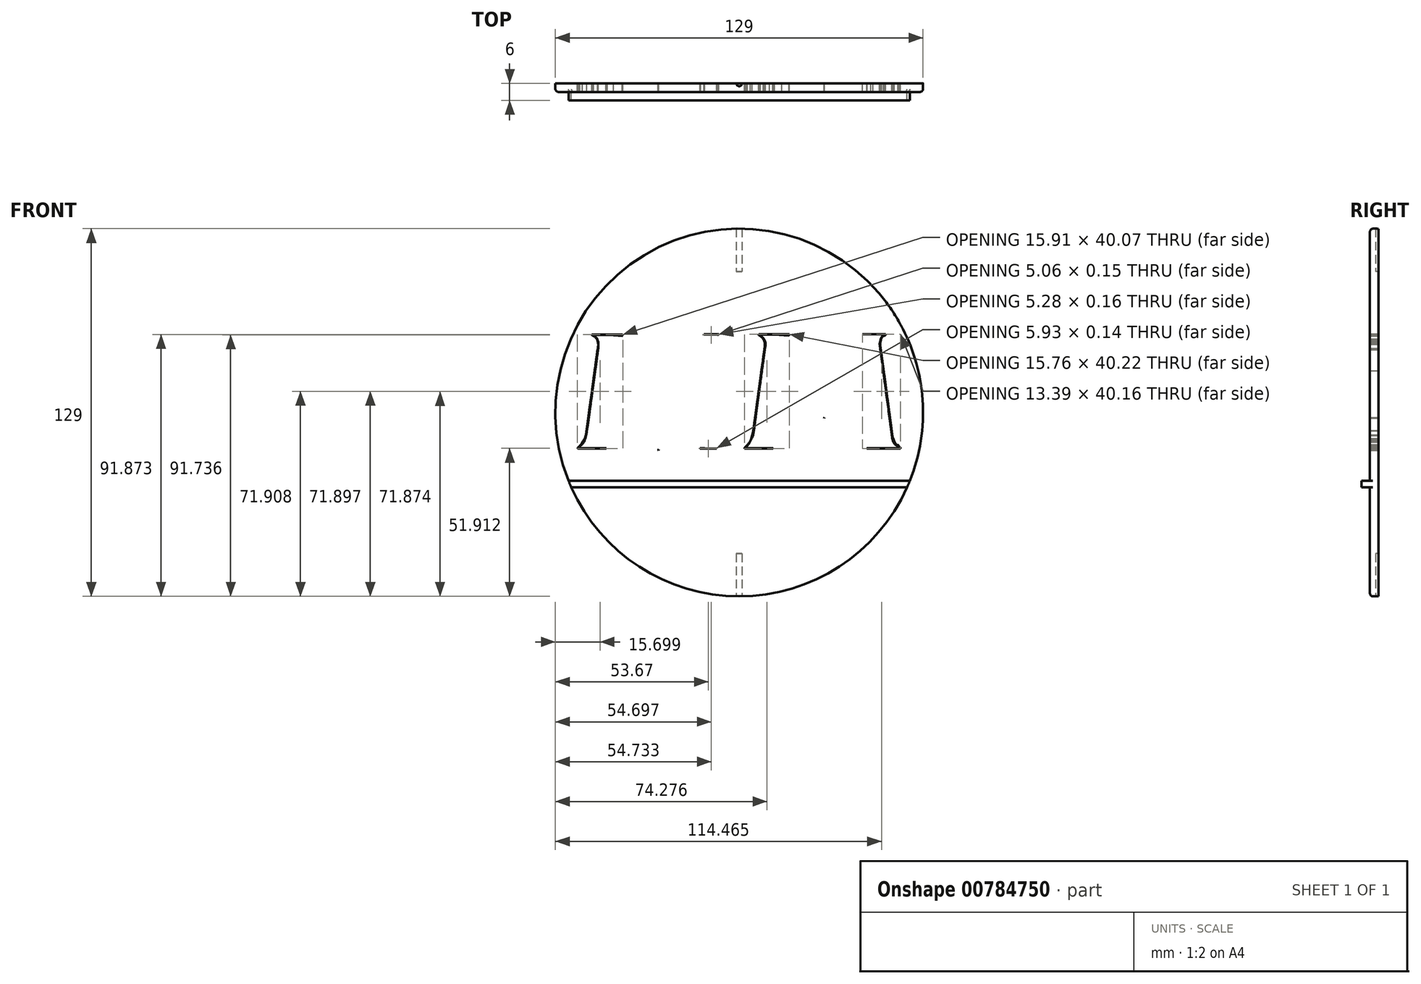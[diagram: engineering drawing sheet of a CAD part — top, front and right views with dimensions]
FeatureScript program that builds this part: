
annotation { "Feature Type Name" : "Feature", "Feature Type Description" : "" }
export const myFeature = defineFeature(function(context is Context, id is Id, definition is map)
    precondition{}
    {
        {
            var Q0;
            Q0=qCreatedBy(makeId("Front.planeOp"),FACE);
            var sketch = newSketch(context, id + "F0", { "sketchPlane" : qUnion([Q0])});
            skLineSegment(sketch, "E0", {"start": v(-46.61, -12.5) * mm, "end": v(-46.61, -12.63) * mm});
            skLineSegment(sketch, "E1", {"start": v(-46.61, -12.63) * mm, "end": v(-51.61, -12.65) * mm});
            skLineSegment(sketch, "E2", {"start": v(-51.61, -12.65) * mm, "end": v(-56.61, -12.66) * mm});
            skLineSegment(sketch, "E3", {"start": v(-56.61, -12.66) * mm, "end": v(-56.7, -12.53) * mm});
            skLineSegment(sketch, "E4", {"start": v(-56.7, -12.53) * mm, "end": v(-46.61, -12.5) * mm});
            skLineSegment(sketch, "E5", {"start": v(-51.66, 27.28) * mm, "end": v(-51.64, 27.4) * mm});
            skLineSegment(sketch, "E6", {"start": v(-51.64, 27.4) * mm, "end": v(-46.26, 27.4) * mm});
            skLineSegment(sketch, "E7", {"start": v(-46.26, 27.4) * mm, "end": v(-40.89, 27.4) * mm});
            skLineSegment(sketch, "E8", {"start": v(-40.89, 27.4) * mm, "end": v(-40.85, 27.03) * mm});
            skLineSegment(sketch, "E9", {"start": v(-40.85, 27.03) * mm, "end": v(-51.66, 27.28) * mm});
            skLineSegment(sketch, "E10", {"start": v(-12.4, 27.45) * mm, "end": v(-7.13, 27.44) * mm});
            skLineSegment(sketch, "E11", {"start": v(-7.13, 27.44) * mm, "end": v(-7.13, 27.3) * mm});
            skLineSegment(sketch, "E12", {"start": v(-7.13, 27.3) * mm, "end": v(-12.4, 27.45) * mm});
            skLineSegment(sketch, "E13", {"start": v(-7.87, -12.66) * mm, "end": v(-13.8, -12.66) * mm});
            skLineSegment(sketch, "E14", {"start": v(-13.8, -12.66) * mm, "end": v(-13.8, -12.52) * mm});
            skLineSegment(sketch, "E15", {"start": v(-13.8, -12.52) * mm, "end": v(-7.87, -12.66) * mm});
            skLineSegment(sketch, "E16", {"start": v(-28.9, -13) * mm, "end": v(-28.9, -13) * mm});
            skLineSegment(sketch, "E17", {"start": v(-7.56, 27.16) * mm, "end": v(-7.28, 27.3) * mm});
            skLineSegment(sketch, "E18", {"start": v(-7.28, 27.3) * mm, "end": v(-12.33, 27.3) * mm});
            skLineSegment(sketch, "E19", {"start": v(-12.33, 27.3) * mm, "end": v(-7.56, 27.16) * mm});
            skLineSegment(sketch, "E20", {"start": v(-41, 26.8) * mm, "end": v(-41.07, 27.3) * mm});
            skLineSegment(sketch, "E21", {"start": v(-41.07, 27.3) * mm, "end": v(-46.25, 27.3) * mm});
            skLineSegment(sketch, "E22", {"start": v(-46.25, 27.3) * mm, "end": v(-41, 26.8) * mm});
            skLineSegment(sketch, "E23", {"start": v(-28.47, -13.11) * mm, "end": v(-28.32, -13.24) * mm});
            skLineSegment(sketch, "E24", {"start": v(-28.32, -13.24) * mm, "end": v(-28.19, -12.9) * mm});
            skLineSegment(sketch, "E25", {"start": v(-28.19, -12.9) * mm, "end": v(-28.47, -13.11) * mm});
            skLineSegment(sketch, "E26", {"start": v(-27.92, -12.22) * mm, "end": v(-27.92, -12.22) * mm});
            skLineSegment(sketch, "E27", {"start": v(11.92, -12.5) * mm, "end": v(11.93, -12.66) * mm});
            skLineSegment(sketch, "E28", {"start": v(11.93, -12.66) * mm, "end": v(6.92, -12.65) * mm});
            skLineSegment(sketch, "E29", {"start": v(6.92, -12.65) * mm, "end": v(1.9, -12.63) * mm});
            skLineSegment(sketch, "E30", {"start": v(1.9, -12.63) * mm, "end": v(1.9, -12.5) * mm});
            skLineSegment(sketch, "E31", {"start": v(1.9, -12.5) * mm, "end": v(11.92, -12.5) * mm});
            skLineSegment(sketch, "E32", {"start": v(12.43, 27.44) * mm, "end": v(17.65, 27.44) * mm});
            skLineSegment(sketch, "E33", {"start": v(17.65, 27.44) * mm, "end": v(17.66, 27.2) * mm});
            skLineSegment(sketch, "E34", {"start": v(17.66, 27.2) * mm, "end": v(12.43, 27.44) * mm});
            skLineSegment(sketch, "E35", {"start": v(29.76, -1.83) * mm, "end": v(29.82, -2) * mm});
            skLineSegment(sketch, "E36", {"start": v(29.82, -2) * mm, "end": v(29.9, -1.79) * mm});
            skLineSegment(sketch, "E37", {"start": v(29.9, -1.79) * mm, "end": v(29.76, -1.83) * mm});
            skLineSegment(sketch, "E38", {"start": v(46.15, 27.45) * mm, "end": v(51.38, 27.44) * mm});
            skLineSegment(sketch, "E39", {"start": v(51.38, 27.44) * mm, "end": v(51.38, 27.3) * mm});
            skLineSegment(sketch, "E40", {"start": v(51.38, 27.3) * mm, "end": v(46.15, 27.45) * mm});
            skLineSegment(sketch, "E41", {"start": v(50.66, -12.65) * mm, "end": v(44.75, -12.63) * mm});
            skLineSegment(sketch, "E42", {"start": v(44.75, -12.63) * mm, "end": v(44.75, -12.5) * mm});
            skLineSegment(sketch, "E43", {"start": v(44.75, -12.5) * mm, "end": v(50.66, -12.65) * mm});
            skLineSegment(sketch, "E44", {"start": v(29.52, -12.91) * mm, "end": v(29.52, -12.91) * mm});
            skLineSegment(sketch, "E45", {"start": v(17.5, 26.99) * mm, "end": v(17.46, 27.32) * mm});
            skLineSegment(sketch, "E46", {"start": v(17.46, 27.32) * mm, "end": v(12.27, 27.32) * mm});
            skLineSegment(sketch, "E47", {"start": v(12.27, 27.32) * mm, "end": v(17.5, 26.99) * mm});
            skLineSegment(sketch, "E48", {"start": v(31.19, -10.73) * mm, "end": v(31.19, -10.73) * mm});
            skLineSegment(sketch, "E49", {"start": v(55.74, -11.44) * mm, "end": v(55.74, -11.44) * mm});
            skLineSegment(sketch, "E50", {"start": v(51.1, -23.94) * mm, "end": v(-0.4, -23.94) * mm});
            skLineSegment(sketch, "E51", {"start": v(-0.4, -23.94) * mm, "end": v(-51.9, -23.94) * mm});
            skFitSpline(sketch, "E52", {"points": [v(48.84, 42.11) * mm, v(51.52, 39.05) * mm, v(54.57, 34.66) * mm, v(56.48, 31.12) * mm]});
            skFitSpline(sketch, "E53", {"points": [v(57.39, 29.43) * mm, v(61.46, 21.5) * mm, v(63.83, 12.79) * mm, v(64.36, 3.78) * mm]});
            skFitSpline(sketch, "E54", {"points": [v(-28.9, -13) * mm, v(-29.65, -12.4) * mm, v(-31.06, -10.96) * mm, v(-31.47, -10.38) * mm]});
            skFitSpline(sketch, "E55", {"points": [v(-31.47, -10.38) * mm, v(-32.14, -9.4) * mm, v(-32.78, -8.19) * mm, v(-33.58, -6.32) * mm]});
            skFitSpline(sketch, "E56", {"points": [v(-33.58, -6.32) * mm, v(-33.81, -5.77) * mm, v(-34.06, -5.2) * mm, v(-34.12, -5.06) * mm]});
            skFitSpline(sketch, "E57", {"points": [v(-34.12, -5.06) * mm, v(-34.24, -4.8) * mm, v(-35.12, -2.7) * mm, v(-35.43, -1.93) * mm]});
            skFitSpline(sketch, "E58", {"points": [v(-35.43, -1.93) * mm, v(-35.52, -1.7) * mm, v(-35.64, -1.45) * mm, v(-35.68, -1.35) * mm]});
            skFitSpline(sketch, "E59", {"points": [v(-35.68, -1.35) * mm, v(-35.73, -1.25) * mm, v(-35.85, -0.95) * mm, v(-35.97, -0.68) * mm]});
            skFitSpline(sketch, "E60", {"points": [v(-35.97, -0.68) * mm, v(-36.36, 0.28) * mm, v(-37.63, 3.3) * mm, v(-37.86, 3.82) * mm]});
            skFitSpline(sketch, "E61", {"points": [v(-37.86, 3.82) * mm, v(-37.93, 3.97) * mm, v(-38.03, 4.22) * mm, v(-38.1, 4.38) * mm]});
            skFitSpline(sketch, "E62", {"points": [v(-38.1, 4.38) * mm, v(-38.16, 4.54) * mm, v(-38.42, 5.17) * mm, v(-38.68, 5.78) * mm]});
            skFitSpline(sketch, "E63", {"points": [v(-38.68, 5.78) * mm, v(-39.72, 8.24) * mm, v(-40.1, 9.15) * mm, v(-40.39, 9.84) * mm]});
            skFitSpline(sketch, "E64", {"points": [v(-40.39, 9.84) * mm, v(-41.15, 11.67) * mm, v(-41.63, 12.8) * mm, v(-41.68, 12.85) * mm]});
            skFitSpline(sketch, "E65", {"points": [v(-41.68, 12.85) * mm, v(-41.7, 12.88) * mm, v(-41.73, 12.95) * mm, v(-41.74, 13) * mm]});
            skFitSpline(sketch, "E66", {"points": [v(-41.74, 13) * mm, v(-41.74, 13.05) * mm, v(-41.79, 13.2) * mm, v(-41.85, 13.32) * mm]});
            skFitSpline(sketch, "E67", {"points": [v(-41.85, 13.32) * mm, v(-41.91, 13.45) * mm, v(-41.96, 13.58) * mm, v(-41.97, 13.6) * mm]});
            skFitSpline(sketch, "E68", {"points": [v(-41.97, 13.6) * mm, v(-41.97, 13.62) * mm, v(-42.04, 13.8) * mm, v(-42.13, 14) * mm]});
            skFitSpline(sketch, "E69", {"points": [v(-42.13, 14) * mm, v(-42.3, 14.35) * mm, v(-42.47, 14.78) * mm, v(-43.2, 16.54) * mm]});
            skFitSpline(sketch, "E70", {"points": [v(-43.2, 16.54) * mm, v(-43.85, 18.08) * mm, v(-43.92, 18.23) * mm, v(-43.95, 18.26) * mm]});
            skFitSpline(sketch, "E71", {"points": [v(-43.95, 18.26) * mm, v(-43.97, 18.28) * mm, v(-44, 18.33) * mm, v(-44, 18.38) * mm]});
            skFitSpline(sketch, "E72", {"points": [v(-44, 18.38) * mm, v(-44.03, 18.51) * mm, v(-45.08, 21.01) * mm, v(-45.1, 21) * mm]});
            skFitSpline(sketch, "E73", {"points": [v(-45.1, 21) * mm, v(-45.11, 20.98) * mm, v(-45.22, 20.17) * mm, v(-45.35, 19.2) * mm]});
            skFitSpline(sketch, "E74", {"points": [v(-45.35, 19.2) * mm, v(-45.56, 17.6) * mm, v(-45.96, 14.62) * mm, v(-46.2, 12.74) * mm]});
            skFitSpline(sketch, "E75", {"points": [v(-46.2, 12.74) * mm, v(-46.26, 12.35) * mm, v(-46.37, 11.46) * mm, v(-46.47, 10.75) * mm]});
            skFitSpline(sketch, "E76", {"points": [v(-46.47, 10.75) * mm, v(-46.75, 8.63) * mm, v(-47.45, 3.3) * mm, v(-47.64, 1.95) * mm]});
            skFitSpline(sketch, "E77", {"points": [v(-47.64, 1.95) * mm, v(-47.73, 1.26) * mm, v(-47.9, -0.03) * mm, v(-48.02, -0.91) * mm]});
            skFitSpline(sketch, "E78", {"points": [v(-48.02, -0.91) * mm, v(-48.13, -1.8) * mm, v(-48.3, -3.1) * mm, v(-48.4, -3.8) * mm]});
            skFitSpline(sketch, "E79", {"points": [v(-48.4, -3.8) * mm, v(-48.83, -7.07) * mm, v(-48.83, -7.04) * mm, v(-48.83, -8.3) * mm]});
            skFitSpline(sketch, "E80", {"points": [v(-48.83, -8.3) * mm, v(-48.84, -9.41) * mm, v(-48.82, -9.58) * mm, v(-48.7, -9.99) * mm]});
            skFitSpline(sketch, "E81", {"points": [v(-48.7, -9.99) * mm, v(-48.55, -10.53) * mm, v(-48.3, -11.04) * mm, v(-48.22, -11) * mm]});
            skFitSpline(sketch, "E82", {"points": [v(-48.22, -11) * mm, v(-48.19, -10.97) * mm, v(-48.16, -11) * mm, v(-48.16, -11.07) * mm]});
            skFitSpline(sketch, "E83", {"points": [v(-48.16, -11.07) * mm, v(-48.16, -11.13) * mm, v(-48.01, -11.33) * mm, v(-47.83, -11.51) * mm]});
            skFitSpline(sketch, "E84", {"points": [v(-47.83, -11.51) * mm, v(-47.44, -11.9) * mm, v(-47.33, -11.97) * mm, v(-46.92, -12.2) * mm]});
            skFitSpline(sketch, "E85", {"points": [v(-46.92, -12.2) * mm, v(-46.68, -12.32) * mm, v(-46.61, -12.39) * mm, v(-46.61, -12.5) * mm]});
            skFitSpline(sketch, "E86", {"points": [v(-56.7, -12.53) * mm, v(-56.74, -12.46) * mm, v(-56.75, -12.41) * mm, v(-56.73, -12.43) * mm]});
            skFitSpline(sketch, "E87", {"points": [v(-56.73, -12.43) * mm, v(-56.7, -12.47) * mm, v(-56.45, -12.23) * mm, v(-55.9, -11.64) * mm]});
            skFitSpline(sketch, "E88", {"points": [v(-55.9, -11.64) * mm, v(-55.62, -11.32) * mm, v(-55.26, -10.83) * mm, v(-55, -10.38) * mm]});
            skFitSpline(sketch, "E89", {"points": [v(-55, -10.38) * mm, v(-54.08, -8.82) * mm, v(-53.69, -7.29) * mm, v(-53.1, -2.93) * mm]});
            skFitSpline(sketch, "E90", {"points": [v(-53.1, -2.93) * mm, v(-53.02, -2.32) * mm, v(-52.9, -1.45) * mm, v(-52.84, -1) * mm]});
            skFitSpline(sketch, "E91", {"points": [v(-52.84, -1) * mm, v(-52.7, 0.06) * mm, v(-52.3, 3.03) * mm, v(-52.1, 4.4) * mm]});
            skFitSpline(sketch, "E92", {"points": [v(-52.1, 4.4) * mm, v(-52.03, 5) * mm, v(-51.92, 5.77) * mm, v(-51.88, 6.1) * mm]});
            skFitSpline(sketch, "E93", {"points": [v(-51.88, 6.1) * mm, v(-51.83, 6.44) * mm, v(-51.72, 7.22) * mm, v(-51.64, 7.83) * mm]});
            skFitSpline(sketch, "E94", {"points": [v(-51.64, 7.83) * mm, v(-51.56, 8.44) * mm, v(-51.45, 9.21) * mm, v(-51.4, 9.55) * mm]});
            skFitSpline(sketch, "E95", {"points": [v(-51.4, 9.55) * mm, v(-51.35, 9.89) * mm, v(-51.24, 10.74) * mm, v(-51.14, 11.45) * mm]});
            skFitSpline(sketch, "E96", {"points": [v(-51.14, 11.45) * mm, v(-50.76, 14.4) * mm, v(-50.68, 14.99) * mm, v(-50.6, 15.54) * mm]});
            skFitSpline(sketch, "E97", {"points": [v(-50.6, 15.54) * mm, v(-50.51, 16.07) * mm, v(-50.34, 17.37) * mm, v(-49.97, 20.13) * mm]});
            skFitSpline(sketch, "E98", {"points": [v(-49.97, 20.13) * mm, v(-49.9, 20.63) * mm, v(-49.82, 21.27) * mm, v(-49.77, 21.56) * mm]});
            skFitSpline(sketch, "E99", {"points": [v(-49.77, 21.56) * mm, v(-49.73, 21.85) * mm, v(-49.66, 22.3) * mm, v(-49.62, 22.56) * mm]});
            skFitSpline(sketch, "E100", {"points": [v(-49.62, 22.56) * mm, v(-49.5, 23.27) * mm, v(-49.52, 24.3) * mm, v(-49.65, 24.75) * mm]});
            skFitSpline(sketch, "E101", {"points": [v(-49.65, 24.75) * mm, v(-49.88, 25.61) * mm, v(-50.54, 26.47) * mm, v(-51.34, 26.95) * mm]});
            skFitSpline(sketch, "E102", {"points": [v(-51.34, 26.95) * mm, v(-51.6, 27.11) * mm, v(-51.67, 27.19) * mm, v(-51.66, 27.28) * mm]});
            skFitSpline(sketch, "E103", {"points": [v(-40.85, 27.03) * mm, v(-40.83, 26.82) * mm, v(-40.77, 26.5) * mm, v(-40.71, 26.31) * mm]});
            skFitSpline(sketch, "E104", {"points": [v(-40.71, 26.31) * mm, v(-40.64, 26.05) * mm, v(-39.7, 23.8) * mm, v(-39.25, 22.8) * mm]});
            skFitSpline(sketch, "E105", {"points": [v(-39.25, 22.8) * mm, v(-39.16, 22.58) * mm, v(-39.04, 22.3) * mm, v(-38.28, 20.51) * mm]});
            skFitSpline(sketch, "E106", {"points": [v(-38.28, 20.51) * mm, v(-37.95, 19.74) * mm, v(-37.65, 19.03) * mm, v(-37.6, 18.93) * mm]});
            skFitSpline(sketch, "E107", {"points": [v(-37.6, 18.93) * mm, v(-37.54, 18.84) * mm, v(-37.5, 18.72) * mm, v(-37.49, 18.68) * mm]});
            skFitSpline(sketch, "E108", {"points": [v(-37.49, 18.68) * mm, v(-37.48, 18.64) * mm, v(-37.26, 18.11) * mm, v(-37, 17.51) * mm]});
            skFitSpline(sketch, "E109", {"points": [v(-37, 17.51) * mm, v(-36.75, 16.91) * mm, v(-36.42, 16.13) * mm, v(-36.27, 15.78) * mm]});
            skFitSpline(sketch, "E110", {"points": [v(-36.27, 15.78) * mm, v(-36.12, 15.42) * mm, v(-35.96, 15.06) * mm, v(-35.92, 14.96) * mm]});
            skFitSpline(sketch, "E111", {"points": [v(-35.92, 14.96) * mm, v(-35.73, 14.54) * mm, v(-35.48, 13.94) * mm, v(-35.48, 13.91) * mm]});
            skFitSpline(sketch, "E112", {"points": [v(-35.48, 13.91) * mm, v(-35.48, 13.9) * mm, v(-35.4, 13.72) * mm, v(-35.3, 13.51) * mm]});
            skFitSpline(sketch, "E113", {"points": [v(-35.3, 13.51) * mm, v(-35.21, 13.31) * mm, v(-34.96, 12.73) * mm, v(-34.75, 12.21) * mm]});
            skFitSpline(sketch, "E114", {"points": [v(-34.75, 12.21) * mm, v(-34.53, 11.7) * mm, v(-34.3, 11.17) * mm, v(-34.25, 11.04) * mm]});
            skFitSpline(sketch, "E115", {"points": [v(-34.25, 11.04) * mm, v(-34.2, 10.91) * mm, v(-33.74, 9.85) * mm, v(-33.24, 8.68) * mm]});
            skFitSpline(sketch, "E116", {"points": [v(-33.24, 8.68) * mm, v(-32.74, 7.5) * mm, v(-32.25, 6.34) * mm, v(-32.15, 6.1) * mm]});
            skFitSpline(sketch, "E117", {"points": [v(-32.15, 6.1) * mm, v(-32.05, 5.86) * mm, v(-31.82, 5.34) * mm, v(-31.65, 4.93) * mm]});
            skFitSpline(sketch, "E118", {"points": [v(-31.65, 4.93) * mm, v(-31.48, 4.53) * mm, v(-31.29, 4.08) * mm, v(-31.22, 3.93) * mm]});
            skFitSpline(sketch, "E119", {"points": [v(-31.22, 3.93) * mm, v(-31.15, 3.78) * mm, v(-31.1, 3.64) * mm, v(-31.1, 3.62) * mm]});
            skFitSpline(sketch, "E120", {"points": [v(-31.1, 3.62) * mm, v(-31.1, 3.6) * mm, v(-31.02, 3.43) * mm, v(-30.92, 3.23) * mm]});
            skFitSpline(sketch, "E121", {"points": [v(-30.92, 3.23) * mm, v(-30.82, 3.03) * mm, v(-30.74, 2.85) * mm, v(-30.74, 2.82) * mm]});
            skFitSpline(sketch, "E122", {"points": [v(-30.74, 2.82) * mm, v(-30.74, 2.8) * mm, v(-30.66, 2.6) * mm, v(-30.57, 2.38) * mm]});
            skFitSpline(sketch, "E123", {"points": [v(-30.57, 2.38) * mm, v(-30.47, 2.16) * mm, v(-30.34, 1.86) * mm, v(-30.28, 1.72) * mm]});
            skFitSpline(sketch, "E124", {"points": [v(-30.28, 1.72) * mm, v(-30.21, 1.57) * mm, v(-29.88, 0.8) * mm, v(-29.54, 0) * mm]});
            skFitSpline(sketch, "E125", {"points": [v(-29.54, 0) * mm, v(-28.7, -1.97) * mm, v(-28.73, -1.9) * mm, v(-28.7, -1.9) * mm]});
            skFitSpline(sketch, "E126", {"points": [v(-28.7, -1.9) * mm, v(-28.68, -1.9) * mm, v(-28.58, -1.67) * mm, v(-28.47, -1.4) * mm]});
            skFitSpline(sketch, "E127", {"points": [v(-28.47, -1.4) * mm, v(-28.36, -1.11) * mm, v(-28.03, -0.25) * mm, v(-27.73, 0.52) * mm]});
            skFitSpline(sketch, "E128", {"points": [v(-27.73, 0.52) * mm, v(-27.42, 1.3) * mm, v(-27.1, 2.13) * mm, v(-27, 2.4) * mm]});
            skFitSpline(sketch, "E129", {"points": [v(-27, 2.4) * mm, v(-26.9, 2.65) * mm, v(-26.8, 2.91) * mm, v(-26.77, 2.98) * mm]});
            skFitSpline(sketch, "E130", {"points": [v(-26.77, 2.98) * mm, v(-26.68, 3.17) * mm, v(-25.65, 5.8) * mm, v(-25.5, 6.22) * mm]});
            skFitSpline(sketch, "E131", {"points": [v(-25.5, 6.22) * mm, v(-25.43, 6.43) * mm, v(-25.34, 6.65) * mm, v(-25.31, 6.72) * mm]});
            skFitSpline(sketch, "E132", {"points": [v(-25.31, 6.72) * mm, v(-25.26, 6.82) * mm, v(-24.61, 8.47) * mm, v(-24.23, 9.46) * mm]});
            skFitSpline(sketch, "E133", {"points": [v(-24.23, 9.46) * mm, v(-24.15, 9.66) * mm, v(-23.92, 10.25) * mm, v(-23.71, 10.78) * mm]});
            skFitSpline(sketch, "E134", {"points": [v(-23.71, 10.78) * mm, v(-23.5, 11.31) * mm, v(-23.22, 12.03) * mm, v(-23.08, 12.39) * mm]});
            skFitSpline(sketch, "E135", {"points": [v(-23.08, 12.39) * mm, v(-22.94, 12.74) * mm, v(-22.82, 13.06) * mm, v(-22.82, 13.09) * mm]});
            skFitSpline(sketch, "E136", {"points": [v(-22.82, 13.09) * mm, v(-22.82, 13.12) * mm, v(-22.74, 13.3) * mm, v(-22.66, 13.5) * mm]});
            skFitSpline(sketch, "E137", {"points": [v(-22.66, 13.5) * mm, v(-22.57, 13.68) * mm, v(-22.5, 13.84) * mm, v(-22.5, 13.85) * mm]});
            skFitSpline(sketch, "E138", {"points": [v(-22.5, 13.85) * mm, v(-22.5, 13.88) * mm, v(-21.46, 16.54) * mm, v(-20.83, 18.14) * mm]});
            skFitSpline(sketch, "E139", {"points": [v(-20.83, 18.14) * mm, v(-20.55, 18.84) * mm, v(-20.25, 19.6) * mm, v(-20.16, 19.84) * mm]});
            skFitSpline(sketch, "E140", {"points": [v(-20.16, 19.84) * mm, v(-20.08, 20.08) * mm, v(-19.72, 20.99) * mm, v(-19.38, 21.85) * mm]});
            skFitSpline(sketch, "E141", {"points": [v(-19.38, 21.85) * mm, v(-18.66, 23.66) * mm, v(-18.1, 25.22) * mm, v(-18.14, 25.26) * mm]});
            skFitSpline(sketch, "E142", {"points": [v(-18.14, 25.26) * mm, v(-18.16, 25.28) * mm, v(-18.15, 25.32) * mm, v(-18.12, 25.36) * mm]});
            skFitSpline(sketch, "E143", {"points": [v(-18.12, 25.36) * mm, v(-18.04, 25.46) * mm, v(-17.83, 26.54) * mm, v(-17.8, 26.99) * mm]});
            skFitSpline(sketch, "E144", {"points": [v(-17.8, 26.99) * mm, v(-17.8, 27.2) * mm, v(-17.76, 27.4) * mm, v(-17.73, 27.43) * mm]});
            skFitSpline(sketch, "E145", {"points": [v(-17.73, 27.43) * mm, v(-17.7, 27.45) * mm, v(-15.3, 27.46) * mm, v(-12.4, 27.45) * mm]});
            skFitSpline(sketch, "E146", {"points": [v(-7.13, 27.3) * mm, v(-7.13, 27.18) * mm, v(-7.2, 27.12) * mm, v(-7.5, 26.97) * mm]});
            skFitSpline(sketch, "E147", {"points": [v(-7.5, 26.97) * mm, v(-7.95, 26.76) * mm, v(-8.22, 26.48) * mm, v(-8.5, 25.98) * mm]});
            skFitSpline(sketch, "E148", {"points": [v(-8.5, 25.98) * mm, v(-8.79, 25.44) * mm, v(-8.94, 24.83) * mm, v(-8.98, 24.1) * mm]});
            skFitSpline(sketch, "E149", {"points": [v(-8.98, 24.1) * mm, v(-9, 23.6) * mm, v(-8.97, 23.2) * mm, v(-8.77, 21.74) * mm]});
            skFitSpline(sketch, "E150", {"points": [v(-8.77, 21.74) * mm, v(-8.64, 20.78) * mm, v(-8.35, 18.62) * mm, v(-8.13, 16.95) * mm]});
            skFitSpline(sketch, "E151", {"points": [v(-8.13, 16.95) * mm, v(-7.9, 15.27) * mm, v(-7.53, 12.53) * mm, v(-7.3, 10.84) * mm]});
            skFitSpline(sketch, "E152", {"points": [v(-7.3, 10.84) * mm, v(-7.07, 9.15) * mm, v(-6.85, 7.5) * mm, v(-6.8, 7.16) * mm]});
            skFitSpline(sketch, "E153", {"points": [v(-6.8, 7.16) * mm, v(-6.76, 6.82) * mm, v(-6.57, 5.34) * mm, v(-6.37, 3.88) * mm]});
            skFitSpline(sketch, "E154", {"points": [v(-6.37, 3.88) * mm, v(-6.17, 2.42) * mm, v(-5.95, 0.75) * mm, v(-5.87, 0.17) * mm]});
            skFitSpline(sketch, "E155", {"points": [v(-5.87, 0.17) * mm, v(-5.8, -0.4) * mm, v(-5.6, -1.78) * mm, v(-5.46, -2.87) * mm]});
            skFitSpline(sketch, "E156", {"points": [v(-5.46, -2.87) * mm, v(-5.31, -3.96) * mm, v(-5.13, -5.34) * mm, v(-5.05, -5.94) * mm]});
            skFitSpline(sketch, "E157", {"points": [v(-5.05, -5.94) * mm, v(-4.77, -8.09) * mm, v(-4.57, -8.97) * mm, v(-4.18, -9.8) * mm]});
            skFitSpline(sketch, "E158", {"points": [v(-4.18, -9.8) * mm, v(-3.96, -10.29) * mm, v(-3.8, -10.58) * mm, v(-3.72, -10.6) * mm]});
            skFitSpline(sketch, "E159", {"points": [v(-3.72, -10.6) * mm, v(-3.7, -10.62) * mm, v(-3.68, -10.65) * mm, v(-3.68, -10.7) * mm]});
            skFitSpline(sketch, "E160", {"points": [v(-3.68, -10.7) * mm, v(-3.68, -10.82) * mm, v(-2.93, -11.56) * mm, v(-2.86, -11.52) * mm]});
            skFitSpline(sketch, "E161", {"points": [v(-2.86, -11.52) * mm, v(-2.81, -11.49) * mm, v(-2.8, -11.5) * mm, v(-2.83, -11.54) * mm]});
            skFitSpline(sketch, "E162", {"points": [v(-2.83, -11.54) * mm, v(-2.86, -11.6) * mm, v(-2.08, -12.3) * mm, v(-1.98, -12.3) * mm]});
            skFitSpline(sketch, "E163", {"points": [v(-1.98, -12.3) * mm, v(-1.92, -12.3) * mm, v(-1.87, -12.48) * mm, v(-1.9, -12.57) * mm]});
            skFitSpline(sketch, "E164", {"points": [v(-1.9, -12.57) * mm, v(-1.94, -12.65) * mm, v(-2.65, -12.66) * mm, v(-7.87, -12.66) * mm]});
            skFitSpline(sketch, "E165", {"points": [v(-13.8, -12.52) * mm, v(-13.8, -12.4) * mm, v(-13.74, -12.35) * mm, v(-13.57, -12.28) * mm]});
            skFitSpline(sketch, "E166", {"points": [v(-13.57, -12.28) * mm, v(-12.57, -11.85) * mm, v(-12.1, -11.4) * mm, v(-11.72, -10.5) * mm]});
            skFitSpline(sketch, "E167", {"points": [v(-11.72, -10.5) * mm, v(-11.5, -10) * mm, v(-11.42, -9.61) * mm, v(-11.34, -8.78) * mm]});
            skFitSpline(sketch, "E168", {"points": [v(-11.34, -8.78) * mm, v(-11.29, -8.27) * mm, v(-11.29, -7.95) * mm, v(-11.33, -7.6) * mm]});
            skFitSpline(sketch, "E169", {"points": [v(-11.33, -7.6) * mm, v(-11.37, -7.35) * mm, v(-11.45, -6.68) * mm, v(-11.51, -6.11) * mm]});
            skFitSpline(sketch, "E170", {"points": [v(-11.51, -6.11) * mm, v(-11.67, -4.72) * mm, v(-12.37, 1.22) * mm, v(-12.6, 3.06) * mm]});
            skFitSpline(sketch, "E171", {"points": [v(-12.6, 3.06) * mm, v(-12.64, 3.47) * mm, v(-12.76, 4.47) * mm, v(-12.86, 5.28) * mm]});
            skFitSpline(sketch, "E172", {"points": [v(-12.86, 5.28) * mm, v(-12.95, 6.1) * mm, v(-13.17, 7.9) * mm, v(-13.33, 9.26) * mm]});
            skFitSpline(sketch, "E173", {"points": [v(-13.33, 9.26) * mm, v(-13.5, 10.63) * mm, v(-13.65, 11.98) * mm, v(-13.68, 12.27) * mm]});
            skFitSpline(sketch, "E174", {"points": [v(-13.68, 12.27) * mm, v(-13.71, 12.56) * mm, v(-13.87, 13.9) * mm, v(-14.03, 15.25) * mm]});
            skFitSpline(sketch, "E175", {"points": [v(-14.03, 15.25) * mm, v(-14.4, 18.45) * mm, v(-14.42, 18.54) * mm, v(-14.55, 19.6) * mm]});
            skFitSpline(sketch, "E176", {"points": [v(-14.55, 19.6) * mm, v(-14.62, 20.1) * mm, v(-14.67, 20.6) * mm, v(-14.67, 20.71) * mm]});
            skFitSpline(sketch, "E177", {"points": [v(-14.67, 20.71) * mm, v(-14.67, 21.09) * mm, v(-14.74, 21.03) * mm, v(-14.95, 20.5) * mm]});
            skFitSpline(sketch, "E178", {"points": [v(-14.95, 20.5) * mm, v(-15.21, 19.8) * mm, v(-15.32, 19.54) * mm, v(-15.38, 19.4) * mm]});
            skFitSpline(sketch, "E179", {"points": [v(-15.38, 19.4) * mm, v(-15.43, 19.28) * mm, v(-16.23, 17.23) * mm, v(-16.45, 16.65) * mm]});
            skFitSpline(sketch, "E180", {"points": [v(-16.45, 16.65) * mm, v(-16.53, 16.46) * mm, v(-16.76, 15.87) * mm, v(-16.97, 15.34) * mm]});
            skFitSpline(sketch, "E181", {"points": [v(-16.97, 15.34) * mm, v(-17.73, 13.4) * mm, v(-17.83, 13.14) * mm, v(-17.83, 13.05) * mm]});
            skFitSpline(sketch, "E182", {"points": [v(-17.83, 13.05) * mm, v(-17.83, 13) * mm, v(-17.85, 12.94) * mm, v(-17.88, 12.91) * mm]});
            skFitSpline(sketch, "E183", {"points": [v(-17.88, 12.91) * mm, v(-17.94, 12.85) * mm, v(-18.87, 10.51) * mm, v(-19.53, 8.76) * mm]});
            skFitSpline(sketch, "E184", {"points": [v(-19.53, 8.76) * mm, v(-19.63, 8.5) * mm, v(-19.73, 8.24) * mm, v(-19.76, 8.18) * mm]});
            skFitSpline(sketch, "E185", {"points": [v(-19.76, 8.18) * mm, v(-19.8, 8.08) * mm, v(-20.38, 6.61) * mm, v(-20.84, 5.43) * mm]});
            skFitSpline(sketch, "E186", {"points": [v(-20.84, 5.43) * mm, v(-20.91, 5.24) * mm, v(-21.19, 4.53) * mm, v(-21.45, 3.85) * mm]});
            skFitSpline(sketch, "E187", {"points": [v(-21.45, 3.85) * mm, v(-21.72, 3.18) * mm, v(-22.05, 2.34) * mm, v(-22.18, 1.98) * mm]});
            skFitSpline(sketch, "E188", {"points": [v(-22.18, 1.98) * mm, v(-22.32, 1.63) * mm, v(-22.66, 0.76) * mm, v(-22.94, 0.05) * mm]});
            skFitSpline(sketch, "E189", {"points": [v(-22.94, 0.05) * mm, v(-23.22, -0.65) * mm, v(-23.53, -1.44) * mm, v(-23.63, -1.7) * mm]});
            skFitSpline(sketch, "E190", {"points": [v(-23.63, -1.7) * mm, v(-23.72, -1.96) * mm, v(-23.85, -2.3) * mm, v(-23.92, -2.46) * mm]});
            skFitSpline(sketch, "E191", {"points": [v(-23.92, -2.46) * mm, v(-23.98, -2.62) * mm, v(-24.06, -2.84) * mm, v(-24.1, -2.96) * mm]});
            skFitSpline(sketch, "E192", {"points": [v(-24.1, -2.96) * mm, v(-24.15, -3.07) * mm, v(-24.29, -3.42) * mm, v(-24.42, -3.75) * mm]});
            skFitSpline(sketch, "E193", {"points": [v(-24.42, -3.75) * mm, v(-24.64, -4.29) * mm, v(-24.94, -5.05) * mm, v(-25.37, -6.2) * mm]});
            skFitSpline(sketch, "E194", {"points": [v(-25.37, -6.2) * mm, v(-25.47, -6.46) * mm, v(-25.57, -6.72) * mm, v(-25.6, -6.79) * mm]});
            skFitSpline(sketch, "E195", {"points": [v(-25.6, -6.79) * mm, v(-25.72, -7.04) * mm, v(-26.2, -8.3) * mm, v(-26.2, -8.37) * mm]});
            skFitSpline(sketch, "E196", {"points": [v(-26.2, -8.37) * mm, v(-26.21, -8.4) * mm, v(-26.26, -8.53) * mm, v(-26.32, -8.64) * mm]});
            skFitSpline(sketch, "E197", {"points": [v(-26.32, -8.64) * mm, v(-26.37, -8.74) * mm, v(-26.51, -9.08) * mm, v(-26.63, -9.39) * mm]});
            skFitSpline(sketch, "E198", {"points": [v(-26.63, -9.39) * mm, v(-26.74, -9.7) * mm, v(-27, -10.36) * mm, v(-27.2, -10.88) * mm]});
            skFitSpline(sketch, "E199", {"points": [v(-27.2, -10.88) * mm, v(-27.73, -12.2) * mm, v(-28.1, -13.13) * mm, v(-28.14, -13.29) * mm]});
            skFitSpline(sketch, "E200", {"points": [v(-28.14, -13.29) * mm, v(-28.16, -13.36) * mm, v(-28.22, -13.42) * mm, v(-28.28, -13.42) * mm]});
            skFitSpline(sketch, "E201", {"points": [v(-28.28, -13.42) * mm, v(-28.33, -13.42) * mm, v(-28.61, -13.23) * mm, v(-28.9, -13) * mm]});
            skFitSpline(sketch, "E202", {"points": [v(-27.92, -12.22) * mm, v(-27.84, -12.03) * mm, v(-27.17, -10.3) * mm, v(-26.42, -8.4) * mm]});
            skFitSpline(sketch, "E203", {"points": [v(-26.42, -8.4) * mm, v(-25.68, -6.48) * mm, v(-24.98, -4.7) * mm, v(-24.87, -4.42) * mm]});
            skFitSpline(sketch, "E204", {"points": [v(-24.87, -4.42) * mm, v(-24.76, -4.15) * mm, v(-24.26, -2.87) * mm, v(-23.76, -1.58) * mm]});
            skFitSpline(sketch, "E205", {"points": [v(-23.76, -1.58) * mm, v(-23.26, -0.3) * mm, v(-22.69, 1.16) * mm, v(-22.5, 1.66) * mm]});
            skFitSpline(sketch, "E206", {"points": [v(-22.5, 1.66) * mm, v(-21.97, 3.01) * mm, v(-21.39, 4.5) * mm, v(-20.95, 5.6) * mm]});
            skFitSpline(sketch, "E207", {"points": [v(-20.95, 5.6) * mm, v(-20.12, 7.74) * mm, v(-17.55, 14.31) * mm, v(-17.15, 15.34) * mm]});
            skFitSpline(sketch, "E208", {"points": [v(-17.15, 15.34) * mm, v(-15.43, 19.77) * mm, v(-14.75, 21.46) * mm, v(-14.69, 21.46) * mm]});
            skFitSpline(sketch, "E209", {"points": [v(-14.69, 21.46) * mm, v(-14.6, 21.46) * mm, v(-14.6, 21.47) * mm, v(-14.35, 19.31) * mm]});
            skFitSpline(sketch, "E210", {"points": [v(-14.35, 19.31) * mm, v(-14.15, 17.57) * mm, v(-13.99, 16.24) * mm, v(-12.6, 4.44) * mm]});
            skFitSpline(sketch, "E211", {"points": [v(-12.6, 4.44) * mm, v(-12.22, 1.29) * mm, v(-11.87, -1.73) * mm, v(-11.8, -2.26) * mm]});
            skFitSpline(sketch, "E212", {"points": [v(-11.8, -2.26) * mm, v(-11.74, -2.79) * mm, v(-11.57, -4.22) * mm, v(-11.43, -5.44) * mm]});
            skFitSpline(sketch, "E213", {"points": [v(-11.43, -5.44) * mm, v(-11.14, -7.83) * mm, v(-11.11, -8.5) * mm, v(-11.25, -9.4) * mm]});
            skFitSpline(sketch, "E214", {"points": [v(-11.25, -9.4) * mm, v(-11.47, -10.84) * mm, v(-12.03, -11.71) * mm, v(-13.1, -12.25) * mm]});
            skFitSpline(sketch, "E215", {"points": [v(-13.1, -12.25) * mm, v(-13.37, -12.38) * mm, v(-13.6, -12.5) * mm, v(-13.61, -12.52) * mm]});
            skFitSpline(sketch, "E216", {"points": [v(-13.61, -12.52) * mm, v(-13.63, -12.53) * mm, v(-11.04, -12.54) * mm, v(-7.87, -12.54) * mm]});
            skFitSpline(sketch, "E217", {"points": [v(-7.87, -12.54) * mm, v(-4.7, -12.54) * mm, v(-2.1, -12.52) * mm, v(-2.1, -12.5) * mm]});
            skFitSpline(sketch, "E218", {"points": [v(-2.1, -12.5) * mm, v(-2.1, -12.47) * mm, v(-2.28, -12.32) * mm, v(-2.5, -12.15) * mm]});
            skFitSpline(sketch, "E219", {"points": [v(-2.5, -12.15) * mm, v(-3.36, -11.5) * mm, v(-4.1, -10.55) * mm, v(-4.43, -9.69) * mm]});
            skFitSpline(sketch, "E220", {"points": [v(-4.43, -9.69) * mm, v(-4.84, -8.63) * mm, v(-4.91, -8.25) * mm, v(-5.52, -3.69) * mm]});
            skFitSpline(sketch, "E221", {"points": [v(-5.52, -3.69) * mm, v(-6.38, 2.78) * mm, v(-6.73, 5.33) * mm, v(-6.9, 6.57) * mm]});
            skFitSpline(sketch, "E222", {"points": [v(-6.9, 6.57) * mm, v(-6.99, 7.26) * mm, v(-7.28, 9.42) * mm, v(-7.54, 11.36) * mm]});
            skFitSpline(sketch, "E223", {"points": [v(-7.54, 11.36) * mm, v(-7.8, 13.3) * mm, v(-8.06, 15.27) * mm, v(-8.12, 15.72) * mm]});
            skFitSpline(sketch, "E224", {"points": [v(-8.12, 15.72) * mm, v(-8.19, 16.17) * mm, v(-8.45, 18.13) * mm, v(-8.71, 20.07) * mm]});
            skFitSpline(sketch, "E225", {"points": [v(-8.71, 20.07) * mm, v(-9.13, 23.15) * mm, v(-9.18, 23.68) * mm, v(-9.15, 24.14) * mm]});
            skFitSpline(sketch, "E226", {"points": [v(-9.15, 24.14) * mm, v(-9.1, 24.8) * mm, v(-8.94, 25.48) * mm, v(-8.7, 25.98) * mm]});
            skFitSpline(sketch, "E227", {"points": [v(-8.7, 25.98) * mm, v(-8.47, 26.44) * mm, v(-7.95, 26.98) * mm, v(-7.56, 27.16) * mm]});
            skFitSpline(sketch, "E228", {"points": [v(-12.33, 27.3) * mm, v(-15.11, 27.32) * mm, v(-17.44, 27.31) * mm, v(-17.51, 27.3) * mm]});
            skFitSpline(sketch, "E229", {"points": [v(-17.51, 27.3) * mm, v(-17.62, 27.27) * mm, v(-17.64, 27.2) * mm, v(-17.67, 26.75) * mm]});
            skFitSpline(sketch, "E230", {"points": [v(-17.67, 26.75) * mm, v(-17.76, 25.61) * mm, v(-18.03, 24.78) * mm, v(-19.84, 20.2) * mm]});
            skFitSpline(sketch, "E231", {"points": [v(-19.84, 20.2) * mm, v(-20.01, 19.76) * mm, v(-20.3, 19.02) * mm, v(-20.49, 18.55) * mm]});
            skFitSpline(sketch, "E232", {"points": [v(-20.49, 18.55) * mm, v(-20.88, 17.53) * mm, v(-21.35, 16.35) * mm, v(-21.95, 14.81) * mm]});
            skFitSpline(sketch, "E233", {"points": [v(-21.95, 14.81) * mm, v(-22.2, 14.19) * mm, v(-22.7, 12.9) * mm, v(-23.07, 11.95) * mm]});
            skFitSpline(sketch, "E234", {"points": [v(-23.07, 11.95) * mm, v(-24.04, 9.46) * mm, v(-24.2, 9.03) * mm, v(-24.57, 8.12) * mm]});
            skFitSpline(sketch, "E235", {"points": [v(-24.57, 8.12) * mm, v(-24.74, 7.67) * mm, v(-25.13, 6.68) * mm, v(-25.42, 5.93) * mm]});
            skFitSpline(sketch, "E236", {"points": [v(-25.42, 5.93) * mm, v(-25.72, 5.17) * mm, v(-26.1, 4.19) * mm, v(-26.28, 3.74) * mm]});
            skFitSpline(sketch, "E237", {"points": [v(-26.28, 3.74) * mm, v(-26.46, 3.29) * mm, v(-27.05, 1.76) * mm, v(-27.6, 0.35) * mm]});
            skFitSpline(sketch, "E238", {"points": [v(-27.6, 0.35) * mm, v(-28.35, -1.55) * mm, v(-28.64, -2.23) * mm, v(-28.71, -2.24) * mm]});
            skFitSpline(sketch, "E239", {"points": [v(-28.71, -2.24) * mm, v(-28.77, -2.26) * mm, v(-28.82, -2.24) * mm, v(-28.82, -2.2) * mm]});
            skFitSpline(sketch, "E240", {"points": [v(-28.82, -2.2) * mm, v(-28.82, -2.18) * mm, v(-29.51, -0.51) * mm, v(-30.37, 1.5) * mm]});
            skFitSpline(sketch, "E241", {"points": [v(-30.37, 1.5) * mm, v(-32.12, 5.6) * mm, v(-32.55, 6.6) * mm, v(-34.34, 10.8) * mm]});
            skFitSpline(sketch, "E242", {"points": [v(-34.34, 10.8) * mm, v(-35.04, 12.45) * mm, v(-35.75, 14.13) * mm, v(-35.93, 14.55) * mm]});
            skFitSpline(sketch, "E243", {"points": [v(-35.93, 14.55) * mm, v(-36.1, 14.97) * mm, v(-36.38, 15.6) * mm, v(-36.53, 15.95) * mm]});
            skFitSpline(sketch, "E244", {"points": [v(-36.53, 15.95) * mm, v(-36.68, 16.3) * mm, v(-37.13, 17.36) * mm, v(-37.53, 18.3) * mm]});
            skFitSpline(sketch, "E245", {"points": [v(-37.53, 18.3) * mm, v(-37.92, 19.22) * mm, v(-38.74, 21.14) * mm, v(-39.35, 22.56) * mm]});
            skFitSpline(sketch, "E246", {"points": [v(-39.35, 22.56) * mm, v(-40.73, 25.78) * mm, v(-40.9, 26.2) * mm, v(-41, 26.8) * mm]});
            skFitSpline(sketch, "E247", {"points": [v(-46.25, 27.3) * mm, v(-49.1, 27.32) * mm, v(-51.44, 27.3) * mm, v(-51.44, 27.27) * mm]});
            skFitSpline(sketch, "E248", {"points": [v(-51.44, 27.27) * mm, v(-51.44, 27.25) * mm, v(-51.27, 27.12) * mm, v(-51.06, 26.98) * mm]});
            skFitSpline(sketch, "E249", {"points": [v(-51.06, 26.98) * mm, v(-50.36, 26.52) * mm, v(-49.87, 25.9) * mm, v(-49.58, 25.1) * mm]});
            skFitSpline(sketch, "E250", {"points": [v(-49.58, 25.1) * mm, v(-49.46, 24.79) * mm, v(-49.43, 24.58) * mm, v(-49.4, 23.93) * mm]});
            skFitSpline(sketch, "E251", {"points": [v(-49.4, 23.93) * mm, v(-49.38, 23.26) * mm, v(-49.4, 22.96) * mm, v(-49.56, 21.89) * mm]});
            skFitSpline(sketch, "E252", {"points": [v(-49.56, 21.89) * mm, v(-49.66, 21.2) * mm, v(-50.07, 18.2) * mm, v(-50.47, 15.22) * mm]});
            skFitSpline(sketch, "E253", {"points": [v(-50.47, 15.22) * mm, v(-50.88, 12.25) * mm, v(-51.5, 7.6) * mm, v(-51.88, 4.88) * mm]});
            skFitSpline(sketch, "E254", {"points": [v(-51.88, 4.88) * mm, v(-52.25, 2.16) * mm, v(-52.64, -0.75) * mm, v(-52.75, -1.58) * mm]});
            skFitSpline(sketch, "E255", {"points": [v(-52.75, -1.58) * mm, v(-53.07, -3.88) * mm, v(-53.3, -5.47) * mm, v(-53.46, -6.35) * mm]});
            skFitSpline(sketch, "E256", {"points": [v(-53.46, -6.35) * mm, v(-53.93, -8.94) * mm, v(-54.66, -10.58) * mm, v(-55.96, -11.94) * mm]});
            skFitSpline(sketch, "E257", {"points": [v(-55.96, -11.94) * mm, v(-56.24, -12.23) * mm, v(-56.46, -12.49) * mm, v(-56.46, -12.5) * mm]});
            skFitSpline(sketch, "E258", {"points": [v(-56.46, -12.5) * mm, v(-56.46, -12.52) * mm, v(-54.28, -12.54) * mm, v(-51.61, -12.54) * mm]});
            skFitSpline(sketch, "E259", {"points": [v(-51.61, -12.54) * mm, v(-48.5, -12.54) * mm, v(-46.76, -12.52) * mm, v(-46.76, -12.48) * mm]});
            skFitSpline(sketch, "E260", {"points": [v(-46.76, -12.48) * mm, v(-46.76, -12.45) * mm, v(-46.79, -12.43) * mm, v(-46.82, -12.43) * mm]});
            skFitSpline(sketch, "E261", {"points": [v(-46.82, -12.43) * mm, v(-46.92, -12.43) * mm, v(-47.48, -12.07) * mm, v(-47.8, -11.8) * mm]});
            skFitSpline(sketch, "E262", {"points": [v(-47.8, -11.8) * mm, v(-48.33, -11.35) * mm, v(-48.74, -10.61) * mm, v(-48.93, -9.77) * mm]});
            skFitSpline(sketch, "E263", {"points": [v(-48.93, -9.77) * mm, v(-49.04, -9.27) * mm, v(-49.03, -7.45) * mm, v(-48.9, -6.43) * mm]});
            skFitSpline(sketch, "E264", {"points": [v(-48.9, -6.43) * mm, v(-48.85, -5.98) * mm, v(-48.58, -3.93) * mm, v(-48.3, -1.88) * mm]});
            skFitSpline(sketch, "E265", {"points": [v(-48.3, -1.88) * mm, v(-48.03, 0.18) * mm, v(-47.62, 3.26) * mm, v(-47.4, 4.96) * mm]});
            skFitSpline(sketch, "E266", {"points": [v(-47.4, 4.96) * mm, v(-47.17, 6.67) * mm, v(-46.82, 9.34) * mm, v(-46.61, 10.9) * mm]});
            skFitSpline(sketch, "E267", {"points": [v(-46.61, 10.9) * mm, v(-46.4, 12.46) * mm, v(-46.1, 14.84) * mm, v(-45.91, 16.19) * mm]});
            skFitSpline(sketch, "E268", {"points": [v(-45.91, 16.19) * mm, v(-45.3, 20.77) * mm, v(-45.23, 21.33) * mm, v(-45.16, 21.37) * mm]});
            skFitSpline(sketch, "E269", {"points": [v(-45.16, 21.37) * mm, v(-45.12, 21.4) * mm, v(-45.07, 21.36) * mm, v(-45.03, 21.28) * mm]});
            skFitSpline(sketch, "E270", {"points": [v(-45.03, 21.28) * mm, v(-45, 21.21) * mm, v(-44.3, 19.58) * mm, v(-43.49, 17.65) * mm]});
            skFitSpline(sketch, "E271", {"points": [v(-43.49, 17.65) * mm, v(-42.68, 15.72) * mm, v(-41.76, 13.55) * mm, v(-41.46, 12.83) * mm]});
            skFitSpline(sketch, "E272", {"points": [v(-41.46, 12.83) * mm, v(-41.15, 12.1) * mm, v(-40.74, 11.12) * mm, v(-40.54, 10.63) * mm]});
            skFitSpline(sketch, "E273", {"points": [v(-40.54, 10.63) * mm, v(-40.33, 10.15) * mm, v(-39.7, 8.65) * mm, v(-39.13, 7.3) * mm]});
            skFitSpline(sketch, "E274", {"points": [v(-39.13, 7.3) * mm, v(-38.57, 5.95) * mm, v(-37.93, 4.44) * mm, v(-37.72, 3.94) * mm]});
            skFitSpline(sketch, "E275", {"points": [v(-37.72, 3.94) * mm, v(-37.5, 3.44) * mm, v(-37.26, 2.86) * mm, v(-37.17, 2.65) * mm]});
            skFitSpline(sketch, "E276", {"points": [v(-37.17, 2.65) * mm, v(-37.08, 2.45) * mm, v(-36.88, 1.96) * mm, v(-36.72, 1.57) * mm]});
            skFitSpline(sketch, "E277", {"points": [v(-36.72, 1.57) * mm, v(-36.56, 1.19) * mm, v(-36.1, 0.1) * mm, v(-35.71, -0.82) * mm]});
            skFitSpline(sketch, "E278", {"points": [v(-35.71, -0.82) * mm, v(-35.32, -1.76) * mm, v(-34.83, -2.91) * mm, v(-34.63, -3.4) * mm]});
            skFitSpline(sketch, "E279", {"points": [v(-34.63, -3.4) * mm, v(-32.5, -8.47) * mm, v(-31.92, -9.61) * mm, v(-30.73, -11.01) * mm]});
            skFitSpline(sketch, "E280", {"points": [v(-30.73, -11.01) * mm, v(-30.3, -11.53) * mm, v(-29.4, -12.38) * mm, v(-28.9, -12.76) * mm]});
            skFitSpline(sketch, "E281", {"points": [v(-28.9, -12.76) * mm, v(-28.74, -12.88) * mm, v(-28.55, -13.04) * mm, v(-28.47, -13.11) * mm]});
            skFitSpline(sketch, "E282", {"points": [v(-28.19, -12.9) * mm, v(-28.1, -12.72) * mm, v(-27.99, -12.41) * mm, v(-27.92, -12.22) * mm]});
            skFitSpline(sketch, "E283", {"points": [v(29.52, -12.91) * mm, v(28.37, -11.96) * mm, v(27.19, -10.68) * mm, v(26.68, -9.81) * mm]});
            skFitSpline(sketch, "E284", {"points": [v(26.68, -9.81) * mm, v(25.96, -8.6) * mm, v(25.35, -7.35) * mm, v(24.52, -5.32) * mm]});
            skFitSpline(sketch, "E285", {"points": [v(24.52, -5.32) * mm, v(24.4, -5.03) * mm, v(24.26, -4.7) * mm, v(24.2, -4.56) * mm]});
            skFitSpline(sketch, "E286", {"points": [v(24.2, -4.56) * mm, v(24.14, -4.44) * mm, v(23.88, -3.82) * mm, v(23.62, -3.2) * mm]});
            skFitSpline(sketch, "E287", {"points": [v(23.62, -3.2) * mm, v(23.35, -2.56) * mm, v(23.1, -1.97) * mm, v(23.05, -1.88) * mm]});
            skFitSpline(sketch, "E288", {"points": [v(23.05, -1.88) * mm, v(23, -1.78) * mm, v(22.93, -1.58) * mm, v(22.88, -1.44) * mm]});
            skFitSpline(sketch, "E289", {"points": [v(22.88, -1.44) * mm, v(22.83, -1.3) * mm, v(22.72, -1.05) * mm, v(22.65, -0.88) * mm]});
            skFitSpline(sketch, "E290", {"points": [v(22.65, -0.88) * mm, v(22.58, -0.72) * mm, v(22.42, -0.35) * mm, v(22.3, -0.06) * mm]});
            skFitSpline(sketch, "E291", {"points": [v(22.3, -0.06) * mm, v(22.18, 0.23) * mm, v(22.05, 0.54) * mm, v(22, 0.64) * mm]});
            skFitSpline(sketch, "E292", {"points": [v(22, 0.64) * mm, v(21.96, 0.73) * mm, v(21.78, 1.17) * mm, v(21.6, 1.6) * mm]});
            skFitSpline(sketch, "E293", {"points": [v(21.6, 1.6) * mm, v(21.42, 2.04) * mm, v(21.2, 2.56) * mm, v(21.1, 2.77) * mm]});
            skFitSpline(sketch, "E294", {"points": [v(21.1, 2.77) * mm, v(21.01, 2.98) * mm, v(20.85, 3.36) * mm, v(20.75, 3.62) * mm]});
            skFitSpline(sketch, "E295", {"points": [v(20.75, 3.62) * mm, v(20.65, 3.88) * mm, v(20.52, 4.2) * mm, v(20.46, 4.32) * mm]});
            skFitSpline(sketch, "E296", {"points": [v(20.46, 4.32) * mm, v(20.4, 4.45) * mm, v(20.22, 4.88) * mm, v(20.05, 5.28) * mm]});
            skFitSpline(sketch, "E297", {"points": [v(20.05, 5.28) * mm, v(19.88, 5.69) * mm, v(19.68, 6.15) * mm, v(19.6, 6.32) * mm]});
            skFitSpline(sketch, "E298", {"points": [v(19.6, 6.32) * mm, v(19.53, 6.5) * mm, v(19.47, 6.64) * mm, v(19.47, 6.66) * mm]});
            skFitSpline(sketch, "E299", {"points": [v(19.47, 6.66) * mm, v(19.47, 6.67) * mm, v(19.4, 6.82) * mm, v(19.33, 7) * mm]});
            skFitSpline(sketch, "E300", {"points": [v(19.33, 7) * mm, v(19.25, 7.16) * mm, v(19.17, 7.37) * mm, v(19.14, 7.45) * mm]});
            skFitSpline(sketch, "E301", {"points": [v(19.14, 7.45) * mm, v(19.12, 7.53) * mm, v(19.03, 7.75) * mm, v(18.94, 7.94) * mm]});
            skFitSpline(sketch, "E302", {"points": [v(18.94, 7.94) * mm, v(18.78, 8.29) * mm, v(18.24, 9.57) * mm, v(17.8, 10.63) * mm]});
            skFitSpline(sketch, "E303", {"points": [v(17.8, 10.63) * mm, v(17.68, 10.92) * mm, v(17.5, 11.36) * mm, v(17.39, 11.6) * mm]});
            skFitSpline(sketch, "E304", {"points": [v(17.39, 11.6) * mm, v(17.28, 11.84) * mm, v(16.97, 12.59) * mm, v(16.69, 13.26) * mm]});
            skFitSpline(sketch, "E305", {"points": [v(16.69, 13.26) * mm, v(16.4, 13.94) * mm, v(16.14, 14.57) * mm, v(16.09, 14.67) * mm]});
            skFitSpline(sketch, "E306", {"points": [v(16.09, 14.67) * mm, v(16.04, 14.76) * mm, v(15.99, 14.89) * mm, v(15.98, 14.95) * mm]});
            skFitSpline(sketch, "E307", {"points": [v(15.98, 14.95) * mm, v(15.97, 15) * mm, v(15.92, 15.13) * mm, v(15.88, 15.21) * mm]});
            skFitSpline(sketch, "E308", {"points": [v(15.88, 15.21) * mm, v(15.83, 15.3) * mm, v(15.68, 15.66) * mm, v(15.53, 16.01) * mm]});
            skFitSpline(sketch, "E309", {"points": [v(15.53, 16.01) * mm, v(15.24, 16.73) * mm, v(14.67, 18.09) * mm, v(14.54, 18.39) * mm]});
            skFitSpline(sketch, "E310", {"points": [v(14.54, 18.39) * mm, v(14.24, 19.08) * mm, v(13.8, 20.12) * mm, v(13.8, 20.15) * mm]});
            skFitSpline(sketch, "E311", {"points": [v(13.8, 20.15) * mm, v(13.8, 20.17) * mm, v(13.72, 20.35) * mm, v(13.63, 20.55) * mm]});
            skFitSpline(sketch, "E312", {"points": [v(13.63, 20.55) * mm, v(13.53, 20.76) * mm, v(13.45, 20.96) * mm, v(13.43, 21) * mm]});
            skFitSpline(sketch, "E313", {"points": [v(13.43, 21) * mm, v(13.42, 21.05) * mm, v(13.35, 20.6) * mm, v(13.28, 20) * mm]});
            skFitSpline(sketch, "E314", {"points": [v(13.28, 20) * mm, v(13.2, 19.42) * mm, v(13.11, 18.7) * mm, v(13.07, 18.4) * mm]});
            skFitSpline(sketch, "E315", {"points": [v(13.07, 18.4) * mm, v(13.03, 18.12) * mm, v(13, 17.82) * mm, v(13, 17.74) * mm]});
            skFitSpline(sketch, "E316", {"points": [v(13, 17.74) * mm, v(12.99, 17.66) * mm, v(12.96, 17.43) * mm, v(12.93, 17.24) * mm]});
            skFitSpline(sketch, "E317", {"points": [v(12.93, 17.24) * mm, v(12.86, 16.83) * mm, v(12.76, 16.13) * mm, v(12.28, 12.45) * mm]});
            skFitSpline(sketch, "E318", {"points": [v(12.28, 12.45) * mm, v(12.08, 10.97) * mm, v(11.88, 9.47) * mm, v(11.84, 9.11) * mm]});
            skFitSpline(sketch, "E319", {"points": [v(11.84, 9.11) * mm, v(11.79, 8.76) * mm, v(11.51, 6.7) * mm, v(11.23, 4.53) * mm]});
            skFitSpline(sketch, "E320", {"points": [v(11.23, 4.53) * mm, v(10.94, 2.35) * mm, v(10.62, -0.03) * mm, v(10.53, -0.76) * mm]});
            skFitSpline(sketch, "E321", {"points": [v(10.53, -0.76) * mm, v(10.43, -1.5) * mm, v(10.27, -2.71) * mm, v(10.17, -3.45) * mm]});
            skFitSpline(sketch, "E322", {"points": [v(10.17, -3.45) * mm, v(10.08, -4.2) * mm, v(9.96, -5.07) * mm, v(9.91, -5.41) * mm]});
            skFitSpline(sketch, "E323", {"points": [v(9.91, -5.41) * mm, v(9.7, -6.9) * mm, v(9.63, -7.84) * mm, v(9.67, -8.69) * mm]});
            skFitSpline(sketch, "E324", {"points": [v(9.67, -8.69) * mm, v(9.7, -9.64) * mm, v(9.79, -10.04) * mm, v(10.1, -10.67) * mm]});
            skFitSpline(sketch, "E325", {"points": [v(10.1, -10.67) * mm, v(10.32, -11.14) * mm, v(10.95, -11.87) * mm, v(11.09, -11.82) * mm]});
            skFitSpline(sketch, "E326", {"points": [v(11.09, -11.82) * mm, v(11.13, -11.8) * mm, v(11.18, -11.82) * mm, v(11.2, -11.85) * mm]});
            skFitSpline(sketch, "E327", {"points": [v(11.2, -11.85) * mm, v(11.23, -11.9) * mm, v(11.21, -11.9) * mm, v(11.16, -11.88) * mm]});
            skFitSpline(sketch, "E328", {"points": [v(11.16, -11.88) * mm, v(11.12, -11.85) * mm, v(11.15, -11.9) * mm, v(11.24, -11.96) * mm]});
            skFitSpline(sketch, "E329", {"points": [v(11.24, -11.96) * mm, v(11.34, -12.03) * mm, v(11.52, -12.15) * mm, v(11.65, -12.22) * mm]});
            skFitSpline(sketch, "E330", {"points": [v(11.65, -12.22) * mm, v(11.84, -12.3) * mm, v(11.9, -12.38) * mm, v(11.92, -12.5) * mm]});
            skFitSpline(sketch, "E331", {"points": [v(1.9, -12.5) * mm, v(1.9, -12.43) * mm, v(2.1, -12.18) * mm, v(2.4, -11.86) * mm]});
            skFitSpline(sketch, "E332", {"points": [v(2.4, -11.86) * mm, v(3.36, -10.85) * mm, v(4.04, -9.63) * mm, v(4.51, -8.04) * mm]});
            skFitSpline(sketch, "E333", {"points": [v(4.51, -8.04) * mm, v(4.77, -7.17) * mm, v(5.12, -5.2) * mm, v(5.47, -2.58) * mm]});
            skFitSpline(sketch, "E334", {"points": [v(5.47, -2.58) * mm, v(5.52, -2.2) * mm, v(5.6, -1.61) * mm, v(5.65, -1.3) * mm]});
            skFitSpline(sketch, "E335", {"points": [v(5.65, -1.3) * mm, v(5.7, -0.97) * mm, v(5.87, 0.39) * mm, v(6.05, 1.72) * mm]});
            skFitSpline(sketch, "E336", {"points": [v(6.05, 1.72) * mm, v(6.23, 3.05) * mm, v(6.4, 4.32) * mm, v(6.43, 4.53) * mm]});
            skFitSpline(sketch, "E337", {"points": [v(6.43, 4.53) * mm, v(6.46, 4.73) * mm, v(6.58, 5.59) * mm, v(6.7, 6.42) * mm]});
            skFitSpline(sketch, "E338", {"points": [v(6.7, 6.42) * mm, v(6.89, 7.88) * mm, v(7.1, 9.41) * mm, v(7.16, 9.84) * mm]});
            skFitSpline(sketch, "E339", {"points": [v(7.16, 9.84) * mm, v(7.2, 10.03) * mm, v(7.4, 11.54) * mm, v(7.54, 12.68) * mm]});
            skFitSpline(sketch, "E340", {"points": [v(7.54, 12.68) * mm, v(7.6, 13.11) * mm, v(7.91, 15.41) * mm, v(8.15, 17.18) * mm]});
            skFitSpline(sketch, "E341", {"points": [v(8.15, 17.18) * mm, v(8.23, 17.76) * mm, v(8.4, 18.92) * mm, v(8.5, 19.75) * mm]});
            skFitSpline(sketch, "E342", {"points": [v(8.5, 19.75) * mm, v(8.62, 20.59) * mm, v(8.77, 21.64) * mm, v(8.83, 22.1) * mm]});
            skFitSpline(sketch, "E343", {"points": [v(8.83, 22.1) * mm, v(9, 23.22) * mm, v(9.03, 23.9) * mm, v(8.95, 24.38) * mm]});
            skFitSpline(sketch, "E344", {"points": [v(8.95, 24.38) * mm, v(8.87, 24.82) * mm, v(8.69, 25.37) * mm, v(8.57, 25.5) * mm]});
            skFitSpline(sketch, "E345", {"points": [v(8.57, 25.5) * mm, v(8.53, 25.56) * mm, v(8.46, 25.68) * mm, v(8.42, 25.77) * mm]});
            skFitSpline(sketch, "E346", {"points": [v(8.42, 25.77) * mm, v(8.29, 26.04) * mm, v(7.61, 26.69) * mm, v(7.2, 26.93) * mm]});
            skFitSpline(sketch, "E347", {"points": [v(7.2, 26.93) * mm, v(6.9, 27.12) * mm, v(6.84, 27.18) * mm, v(6.88, 27.28) * mm]});
            skFitSpline(sketch, "E348", {"points": [v(6.88, 27.28) * mm, v(6.92, 27.44) * mm, v(7.02, 27.5) * mm, v(7.12, 27.47) * mm]});
            skFitSpline(sketch, "E349", {"points": [v(7.12, 27.47) * mm, v(7.17, 27.45) * mm, v(9.55, 27.44) * mm, v(12.43, 27.44) * mm]});
            skFitSpline(sketch, "E350", {"points": [v(17.66, 27.2) * mm, v(17.66, 26.75) * mm, v(17.89, 25.96) * mm, v(18.24, 25.2) * mm]});
            skFitSpline(sketch, "E351", {"points": [v(18.24, 25.2) * mm, v(18.33, 24.98) * mm, v(18.41, 24.8) * mm, v(18.41, 24.78) * mm]});
            skFitSpline(sketch, "E352", {"points": [v(18.41, 24.78) * mm, v(18.41, 24.77) * mm, v(18.5, 24.56) * mm, v(18.61, 24.33) * mm]});
            skFitSpline(sketch, "E353", {"points": [v(18.61, 24.33) * mm, v(18.72, 24.1) * mm, v(18.9, 23.7) * mm, v(19, 23.45) * mm]});
            skFitSpline(sketch, "E354", {"points": [v(19, 23.45) * mm, v(19.1, 23.2) * mm, v(19.35, 22.6) * mm, v(19.56, 22.1) * mm]});
            skFitSpline(sketch, "E355", {"points": [v(19.56, 22.1) * mm, v(19.77, 21.62) * mm, v(20.04, 20.99) * mm, v(20.15, 20.72) * mm]});
            skFitSpline(sketch, "E356", {"points": [v(20.15, 20.72) * mm, v(20.26, 20.44) * mm, v(20.6, 19.65) * mm, v(20.9, 18.96) * mm]});
            skFitSpline(sketch, "E357", {"points": [v(20.9, 18.96) * mm, v(21.2, 18.27) * mm, v(21.65, 17.2) * mm, v(21.9, 16.6) * mm]});
            skFitSpline(sketch, "E358", {"points": [v(21.9, 16.6) * mm, v(22.17, 15.98) * mm, v(22.52, 15.17) * mm, v(22.68, 14.78) * mm]});
            skFitSpline(sketch, "E359", {"points": [v(22.68, 14.78) * mm, v(22.85, 14.4) * mm, v(23.03, 13.96) * mm, v(23.1, 13.82) * mm]});
            skFitSpline(sketch, "E360", {"points": [v(23.1, 13.82) * mm, v(23.25, 13.44) * mm, v(23.53, 12.78) * mm, v(23.66, 12.47) * mm]});
            skFitSpline(sketch, "E361", {"points": [v(23.66, 12.47) * mm, v(23.73, 12.33) * mm, v(23.92, 11.88) * mm, v(24.09, 11.48) * mm]});
            skFitSpline(sketch, "E362", {"points": [v(24.09, 11.48) * mm, v(24.25, 11.08) * mm, v(24.52, 10.46) * mm, v(24.67, 10.1) * mm]});
            skFitSpline(sketch, "E363", {"points": [v(24.67, 10.1) * mm, v(24.82, 9.75) * mm, v(25.32, 8.58) * mm, v(25.78, 7.5) * mm]});
            skFitSpline(sketch, "E364", {"points": [v(25.78, 7.5) * mm, v(26.48, 5.86) * mm, v(27.38, 3.74) * mm, v(27.68, 3.03) * mm]});
            skFitSpline(sketch, "E365", {"points": [v(27.68, 3.03) * mm, v(27.72, 2.94) * mm, v(27.85, 2.65) * mm, v(27.96, 2.4) * mm]});
            skFitSpline(sketch, "E366", {"points": [v(27.96, 2.4) * mm, v(28.07, 2.13) * mm, v(28.3, 1.6) * mm, v(28.46, 1.22) * mm]});
            skFitSpline(sketch, "E367", {"points": [v(28.46, 1.22) * mm, v(28.9, 0.15) * mm, v(29.46, -1.15) * mm, v(29.59, -1.42) * mm]});
            skFitSpline(sketch, "E368", {"points": [v(29.59, -1.42) * mm, v(29.65, -1.56) * mm, v(29.73, -1.74) * mm, v(29.76, -1.83) * mm]});
            skFitSpline(sketch, "E369", {"points": [v(29.9, -1.79) * mm, v(29.94, -1.68) * mm, v(30.21, -0.97) * mm, v(30.51, -0.2) * mm]});
            skFitSpline(sketch, "E370", {"points": [v(30.51, -0.2) * mm, v(30.8, 0.55) * mm, v(31.11, 1.32) * mm, v(31.19, 1.51) * mm]});
            skFitSpline(sketch, "E371", {"points": [v(31.19, 1.51) * mm, v(31.26, 1.7) * mm, v(31.55, 2.44) * mm, v(31.83, 3.15) * mm]});
            skFitSpline(sketch, "E372", {"points": [v(31.83, 3.15) * mm, v(32.1, 3.86) * mm, v(32.4, 4.6) * mm, v(32.48, 4.82) * mm]});
            skFitSpline(sketch, "E373", {"points": [v(32.48, 4.82) * mm, v(32.56, 5.03) * mm, v(32.66, 5.29) * mm, v(32.7, 5.4) * mm]});
            skFitSpline(sketch, "E374", {"points": [v(32.7, 5.4) * mm, v(32.97, 6.07) * mm, v(33.82, 8.24) * mm, v(33.94, 8.56) * mm]});
            skFitSpline(sketch, "E375", {"points": [v(33.94, 8.56) * mm, v(34.02, 8.77) * mm, v(34.13, 9.03) * mm, v(34.17, 9.13) * mm]});
            skFitSpline(sketch, "E376", {"points": [v(34.17, 9.13) * mm, v(34.22, 9.24) * mm, v(34.24, 9.35) * mm, v(34.23, 9.38) * mm]});
            skFitSpline(sketch, "E377", {"points": [v(34.23, 9.38) * mm, v(34.21, 9.4) * mm, v(34.22, 9.43) * mm, v(34.24, 9.44) * mm]});
            skFitSpline(sketch, "E378", {"points": [v(34.24, 9.44) * mm, v(34.3, 9.47) * mm, v(34.82, 10.79) * mm, v(35.8, 13.32) * mm]});
            skFitSpline(sketch, "E379", {"points": [v(35.8, 13.32) * mm, v(35.95, 13.7) * mm, v(36.15, 14.2) * mm, v(36.24, 14.43) * mm]});
            skFitSpline(sketch, "E380", {"points": [v(36.24, 14.43) * mm, v(36.34, 14.66) * mm, v(36.5, 15.1) * mm, v(36.62, 15.4) * mm]});
            skFitSpline(sketch, "E381", {"points": [v(36.62, 15.4) * mm, v(36.74, 15.7) * mm, v(36.87, 16.04) * mm, v(36.92, 16.16) * mm]});
            skFitSpline(sketch, "E382", {"points": [v(36.92, 16.16) * mm, v(37.01, 16.4) * mm, v(37.08, 16.65) * mm, v(37.07, 16.68) * mm]});
            skFitSpline(sketch, "E383", {"points": [v(37.07, 16.68) * mm, v(37.06, 16.69) * mm, v(37.08, 16.72) * mm, v(37.1, 16.74) * mm]});
            skFitSpline(sketch, "E384", {"points": [v(37.1, 16.74) * mm, v(37.15, 16.77) * mm, v(37.63, 17.95) * mm, v(38.27, 19.64) * mm]});
            skFitSpline(sketch, "E385", {"points": [v(38.27, 19.64) * mm, v(38.38, 19.92) * mm, v(38.62, 20.52) * mm, v(38.79, 20.95) * mm]});
            skFitSpline(sketch, "E386", {"points": [v(38.79, 20.95) * mm, v(39.05, 21.62) * mm, v(39.56, 22.93) * mm, v(39.84, 23.64) * mm]});
            skFitSpline(sketch, "E387", {"points": [v(39.84, 23.64) * mm, v(40.33, 24.9) * mm, v(40.57, 25.76) * mm, v(40.68, 26.67) * mm]});
            skFitSpline(sketch, "E388", {"points": [v(40.68, 26.67) * mm, v(40.75, 27.2) * mm, v(40.8, 27.47) * mm, v(40.85, 27.46) * mm]});
            skFitSpline(sketch, "E389", {"points": [v(40.85, 27.46) * mm, v(40.89, 27.46) * mm, v(43.27, 27.45) * mm, v(46.15, 27.45) * mm]});
            skFitSpline(sketch, "E390", {"points": [v(51.38, 27.3) * mm, v(51.38, 27.19) * mm, v(51.32, 27.13) * mm, v(51.05, 27) * mm]});
            skFitSpline(sketch, "E391", {"points": [v(51.05, 27) * mm, v(50.39, 26.67) * mm, v(49.9, 25.96) * mm, v(49.65, 24.98) * mm]});
            skFitSpline(sketch, "E392", {"points": [v(49.65, 24.98) * mm, v(49.5, 24.36) * mm, v(49.51, 23.4) * mm, v(49.7, 22.06) * mm]});
            skFitSpline(sketch, "E393", {"points": [v(49.7, 22.06) * mm, v(49.78, 21.47) * mm, v(50.04, 19.59) * mm, v(50.27, 17.88) * mm]});
            skFitSpline(sketch, "E394", {"points": [v(50.27, 17.88) * mm, v(50.5, 16.18) * mm, v(50.7, 14.7) * mm, v(50.7, 14.6) * mm]});
            skFitSpline(sketch, "E395", {"points": [v(50.7, 14.6) * mm, v(50.72, 14.51) * mm, v(50.79, 14.04) * mm, v(50.85, 13.56) * mm]});
            skFitSpline(sketch, "E396", {"points": [v(50.85, 13.56) * mm, v(50.92, 13.07) * mm, v(51.09, 11.78) * mm, v(51.24, 10.7) * mm]});
            skFitSpline(sketch, "E397", {"points": [v(51.24, 10.7) * mm, v(51.38, 9.6) * mm, v(51.57, 8.22) * mm, v(51.65, 7.62) * mm]});
            skFitSpline(sketch, "E398", {"points": [v(51.65, 7.62) * mm, v(51.89, 5.85) * mm, v(52.31, 2.72) * mm, v(52.38, 2.22) * mm]});
            skFitSpline(sketch, "E399", {"points": [v(52.38, 2.22) * mm, v(52.41, 1.96) * mm, v(52.61, 0.49) * mm, v(52.82, -1.06) * mm]});
            skFitSpline(sketch, "E400", {"points": [v(52.82, -1.06) * mm, v(53.02, -2.6) * mm, v(53.24, -4.26) * mm, v(53.31, -4.74) * mm]});
            skFitSpline(sketch, "E401", {"points": [v(53.31, -4.74) * mm, v(53.38, -5.22) * mm, v(53.48, -6.01) * mm, v(53.54, -6.5) * mm]});
            skFitSpline(sketch, "E402", {"points": [v(53.54, -6.5) * mm, v(53.7, -7.63) * mm, v(53.93, -8.83) * mm, v(54.08, -9.13) * mm]});
            skFitSpline(sketch, "E403", {"points": [v(54.08, -9.13) * mm, v(54.14, -9.26) * mm, v(54.19, -9.4) * mm, v(54.19, -9.45) * mm]});
            skFitSpline(sketch, "E404", {"points": [v(54.19, -9.45) * mm, v(54.19, -9.5) * mm, v(54.29, -9.73) * mm, v(54.41, -9.98) * mm]});
            skFitSpline(sketch, "E405", {"points": [v(54.41, -9.98) * mm, v(54.83, -10.8) * mm, v(55.34, -11.39) * mm, v(56.18, -12.03) * mm]});
            skFitSpline(sketch, "E406", {"points": [v(56.18, -12.03) * mm, v(56.6, -12.35) * mm, v(56.66, -12.43) * mm, v(56.6, -12.57) * mm]});
            skFitSpline(sketch, "E407", {"points": [v(56.6, -12.57) * mm, v(56.58, -12.65) * mm, v(56.02, -12.66) * mm, v(50.66, -12.65) * mm]});
            skFitSpline(sketch, "E408", {"points": [v(44.75, -12.5) * mm, v(44.75, -12.39) * mm, v(44.8, -12.33) * mm, v(44.98, -12.26) * mm]});
            skFitSpline(sketch, "E409", {"points": [v(44.98, -12.26) * mm, v(45.96, -11.87) * mm, v(46.59, -11.2) * mm, v(46.92, -10.24) * mm]});
            skFitSpline(sketch, "E410", {"points": [v(46.92, -10.24) * mm, v(47, -10.01) * mm, v(47.1, -9.47) * mm, v(47.16, -9.04) * mm]});
            skFitSpline(sketch, "E411", {"points": [v(47.16, -9.04) * mm, v(47.26, -8.16) * mm, v(47.26, -8.16) * mm, v(46.88, -4.94) * mm]});
            skFitSpline(sketch, "E412", {"points": [v(46.88, -4.94) * mm, v(46.25, 0.3) * mm, v(46.11, 1.5) * mm, v(46, 2.42) * mm]});
            skFitSpline(sketch, "E413", {"points": [v(46, 2.42) * mm, v(45.94, 2.98) * mm, v(45.8, 4.22) * mm, v(45.68, 5.17) * mm]});
            skFitSpline(sketch, "E414", {"points": [v(45.68, 5.17) * mm, v(45.43, 7.3) * mm, v(45.28, 8.52) * mm, v(45.1, 10.12) * mm]});
            skFitSpline(sketch, "E415", {"points": [v(45.1, 10.12) * mm, v(45.02, 10.8) * mm, v(44.83, 12.37) * mm, v(44.69, 13.6) * mm]});
            skFitSpline(sketch, "E416", {"points": [v(44.69, 13.6) * mm, v(44.54, 14.83) * mm, v(44.4, 16.03) * mm, v(44.37, 16.27) * mm]});
            skFitSpline(sketch, "E417", {"points": [v(44.37, 16.27) * mm, v(44.34, 16.52) * mm, v(44.26, 17.17) * mm, v(44.2, 17.74) * mm]});
            skFitSpline(sketch, "E418", {"points": [v(44.2, 17.74) * mm, v(44.12, 18.3) * mm, v(44.03, 19.11) * mm, v(43.98, 19.55) * mm]});
            skFitSpline(sketch, "E419", {"points": [v(43.98, 19.55) * mm, v(43.93, 19.98) * mm, v(43.88, 20.47) * mm, v(43.86, 20.64) * mm]});
            skFitSpline(sketch, "E420", {"points": [v(43.86, 20.64) * mm, v(43.84, 20.81) * mm, v(43.8, 20.95) * mm, v(43.78, 20.95) * mm]});
            skFitSpline(sketch, "E421", {"points": [v(43.78, 20.95) * mm, v(43.76, 20.95) * mm, v(43.67, 20.76) * mm, v(43.58, 20.53) * mm]});
            skFitSpline(sketch, "E422", {"points": [v(43.58, 20.53) * mm, v(43.4, 20.06) * mm, v(43.17, 19.47) * mm, v(42.41, 17.53) * mm]});
            skFitSpline(sketch, "E423", {"points": [v(42.41, 17.53) * mm, v(42.13, 16.82) * mm, v(41.83, 16.03) * mm, v(41.73, 15.78) * mm]});
            skFitSpline(sketch, "E424", {"points": [v(41.73, 15.78) * mm, v(41.46, 15.07) * mm, v(41.38, 14.86) * mm, v(41.3, 14.67) * mm]});
            skFitSpline(sketch, "E425", {"points": [v(41.3, 14.67) * mm, v(41.13, 14.27) * mm, v(40.14, 11.72) * mm, v(40.13, 11.66) * mm]});
            skFitSpline(sketch, "E426", {"points": [v(40.13, 11.66) * mm, v(40.13, 11.64) * mm, v(40.08, 11.54) * mm, v(40.03, 11.42) * mm]});
            skFitSpline(sketch, "E427", {"points": [v(40.03, 11.42) * mm, v(39.94, 11.2) * mm, v(39.68, 10.54) * mm, v(38.71, 8.06) * mm]});
            skFitSpline(sketch, "E428", {"points": [v(38.71, 8.06) * mm, v(38.66, 7.93) * mm, v(38.59, 7.74) * mm, v(38.54, 7.64) * mm]});
            skFitSpline(sketch, "E429", {"points": [v(38.54, 7.64) * mm, v(38.5, 7.54) * mm, v(38.46, 7.43) * mm, v(38.46, 7.4) * mm]});
            skFitSpline(sketch, "E430", {"points": [v(38.46, 7.4) * mm, v(38.46, 7.36) * mm, v(38.44, 7.28) * mm, v(38.4, 7.23) * mm]});
            skFitSpline(sketch, "E431", {"points": [v(38.4, 7.23) * mm, v(38.35, 7.13) * mm, v(37.8, 5.73) * mm, v(37.46, 4.85) * mm]});
            skFitSpline(sketch, "E432", {"points": [v(37.46, 4.85) * mm, v(37.24, 4.27) * mm, v(37.14, 4) * mm, v(36.84, 3.27) * mm]});
            skFitSpline(sketch, "E433", {"points": [v(36.84, 3.27) * mm, v(36.71, 2.95) * mm, v(36.54, 2.5) * mm, v(36.45, 2.27) * mm]});
            skFitSpline(sketch, "E434", {"points": [v(36.45, 2.27) * mm, v(36.25, 1.76) * mm, v(36.1, 1.37) * mm, v(35.7, 0.35) * mm]});
            skFitSpline(sketch, "E435", {"points": [v(35.7, 0.35) * mm, v(35.28, -0.73) * mm, v(34.62, -2.43) * mm, v(34.22, -3.45) * mm]});
            skFitSpline(sketch, "E436", {"points": [v(34.22, -3.45) * mm, v(34.04, -3.9) * mm, v(33.84, -4.42) * mm, v(33.76, -4.6) * mm]});
            skFitSpline(sketch, "E437", {"points": [v(33.76, -4.6) * mm, v(33.68, -4.78) * mm, v(33.61, -4.95) * mm, v(33.61, -4.97) * mm]});
            skFitSpline(sketch, "E438", {"points": [v(33.61, -4.97) * mm, v(33.61, -5.01) * mm, v(33.32, -5.78) * mm, v(33.08, -6.38) * mm]});
            skFitSpline(sketch, "E439", {"points": [v(33.08, -6.38) * mm, v(33.06, -6.44) * mm, v(32.98, -6.64) * mm, v(32.9, -6.81) * mm]});
            skFitSpline(sketch, "E440", {"points": [v(32.9, -6.81) * mm, v(32.84, -7) * mm, v(32.75, -7.22) * mm, v(32.7, -7.31) * mm]});
            skFitSpline(sketch, "E441", {"points": [v(32.7, -7.31) * mm, v(32.47, -7.88) * mm, v(31.74, -9.8) * mm, v(31.74, -9.86) * mm]});
            skFitSpline(sketch, "E442", {"points": [v(31.74, -9.86) * mm, v(31.74, -9.91) * mm, v(31.72, -9.97) * mm, v(31.69, -10) * mm]});
            skFitSpline(sketch, "E443", {"points": [v(31.69, -10) * mm, v(31.66, -10.03) * mm, v(31.57, -10.23) * mm, v(31.49, -10.44) * mm]});
            skFitSpline(sketch, "E444", {"points": [v(31.49, -10.44) * mm, v(31.4, -10.65) * mm, v(31.14, -11.33) * mm, v(30.9, -11.96) * mm]});
            skFitSpline(sketch, "E445", {"points": [v(30.9, -11.96) * mm, v(30.65, -12.59) * mm, v(30.42, -13.17) * mm, v(30.39, -13.26) * mm]});
            skFitSpline(sketch, "E446", {"points": [v(30.39, -13.26) * mm, v(30.35, -13.35) * mm, v(30.28, -13.42) * mm, v(30.23, -13.42) * mm]});
            skFitSpline(sketch, "E447", {"points": [v(30.23, -13.42) * mm, v(30.18, -13.42) * mm, v(29.86, -13.2) * mm, v(29.52, -12.91) * mm]});
            skFitSpline(sketch, "E448", {"points": [v(31.19, -10.73) * mm, v(32.75, -6.7) * mm, v(33.15, -5.69) * mm, v(33.85, -3.92) * mm]});
            skFitSpline(sketch, "E449", {"points": [v(33.85, -3.92) * mm, v(34.1, -3.28) * mm, v(35, -1) * mm, v(35.84, 1.16) * mm]});
            skFitSpline(sketch, "E450", {"points": [v(35.84, 1.16) * mm, v(36.68, 3.32) * mm, v(37.64, 5.8) * mm, v(37.98, 6.66) * mm]});
            skFitSpline(sketch, "E451", {"points": [v(37.98, 6.66) * mm, v(38.32, 7.53) * mm, v(38.67, 8.42) * mm, v(38.76, 8.65) * mm]});
            skFitSpline(sketch, "E452", {"points": [v(38.76, 8.65) * mm, v(38.84, 8.87) * mm, v(39.5, 10.55) * mm, v(40.22, 12.39) * mm]});
            skFitSpline(sketch, "E453", {"points": [v(40.22, 12.39) * mm, v(42.37, 17.88) * mm, v(43.31, 20.3) * mm, v(43.53, 20.88) * mm]});
            skFitSpline(sketch, "E454", {"points": [v(43.53, 20.88) * mm, v(43.69, 21.28) * mm, v(43.77, 21.42) * mm, v(43.83, 21.4) * mm]});
            skFitSpline(sketch, "E455", {"points": [v(43.83, 21.4) * mm, v(43.91, 21.4) * mm, v(44.01, 20.66) * mm, v(44.46, 16.83) * mm]});
            skFitSpline(sketch, "E456", {"points": [v(44.46, 16.83) * mm, v(44.76, 14.32) * mm, v(45.24, 10.24) * mm, v(45.53, 7.77) * mm]});
            skFitSpline(sketch, "E457", {"points": [v(45.53, 7.77) * mm, v(45.83, 5.3) * mm, v(46.29, 1.39) * mm, v(46.56, -0.91) * mm]});
            skFitSpline(sketch, "E458", {"points": [v(46.56, -0.91) * mm, v(46.83, -3.2) * mm, v(47.12, -5.66) * mm, v(47.2, -6.35) * mm]});
            skFitSpline(sketch, "E459", {"points": [v(47.2, -6.35) * mm, v(47.54, -9.07) * mm, v(47.26, -10.65) * mm, v(46.27, -11.64) * mm]});
            skFitSpline(sketch, "E460", {"points": [v(46.27, -11.64) * mm, v(46.02, -11.9) * mm, v(45.78, -12.06) * mm, v(45.44, -12.23) * mm]});
            skFitSpline(sketch, "E461", {"points": [v(45.44, -12.23) * mm, v(45.18, -12.35) * mm, v(44.96, -12.47) * mm, v(44.96, -12.5) * mm]});
            skFitSpline(sketch, "E462", {"points": [v(44.96, -12.5) * mm, v(44.95, -12.52) * mm, v(47.53, -12.54) * mm, v(50.68, -12.54) * mm]});
            skFitSpline(sketch, "E463", {"points": [v(50.68, -12.54) * mm, v(53.88, -12.54) * mm, v(56.4, -12.52) * mm, v(56.4, -12.5) * mm]});
            skFitSpline(sketch, "E464", {"points": [v(56.4, -12.5) * mm, v(56.4, -12.46) * mm, v(56.26, -12.33) * mm, v(56.07, -12.19) * mm]});
            skFitSpline(sketch, "E465", {"points": [v(56.07, -12.19) * mm, v(54.67, -11.13) * mm, v(53.92, -9.82) * mm, v(53.58, -7.8) * mm]});
            skFitSpline(sketch, "E466", {"points": [v(53.58, -7.8) * mm, v(53.53, -7.54) * mm, v(53.24, -5.43) * mm, v(52.93, -3.13) * mm]});
            skFitSpline(sketch, "E467", {"points": [v(52.93, -3.13) * mm, v(52.27, 1.81) * mm, v(51.87, 4.8) * mm, v(51.15, 10.14) * mm]});
            skFitSpline(sketch, "E468", {"points": [v(51.15, 10.14) * mm, v(50.86, 12.3) * mm, v(50.5, 14.95) * mm, v(50.36, 16.01) * mm]});
            skFitSpline(sketch, "E469", {"points": [v(50.36, 16.01) * mm, v(50.22, 17.07) * mm, v(49.93, 19.23) * mm, v(49.71, 20.8) * mm]});
            skFitSpline(sketch, "E470", {"points": [v(49.71, 20.8) * mm, v(49.29, 23.95) * mm, v(49.28, 24.13) * mm, v(49.52, 25.1) * mm]});
            skFitSpline(sketch, "E471", {"points": [v(49.52, 25.1) * mm, v(49.75, 26.06) * mm, v(50.25, 26.8) * mm, v(50.85, 27.1) * mm]});
            skFitSpline(sketch, "E472", {"points": [v(50.85, 27.1) * mm, v(51.01, 27.17) * mm, v(51.15, 27.25) * mm, v(51.15, 27.28) * mm]});
            skFitSpline(sketch, "E473", {"points": [v(51.15, 27.28) * mm, v(51.15, 27.33) * mm, v(41.03, 27.33) * mm, v(40.94, 27.28) * mm]});
            skFitSpline(sketch, "E474", {"points": [v(40.94, 27.28) * mm, v(40.9, 27.25) * mm, v(40.86, 27) * mm, v(40.84, 26.7) * mm]});
            skFitSpline(sketch, "E475", {"points": [v(40.84, 26.7) * mm, v(40.8, 26.1) * mm, v(40.56, 25.12) * mm, v(40.23, 24.2) * mm]});
            skFitSpline(sketch, "E476", {"points": [v(40.23, 24.2) * mm, v(40.01, 23.6) * mm, v(39.84, 23.14) * mm, v(38.7, 20.25) * mm]});
            skFitSpline(sketch, "E477", {"points": [v(38.7, 20.25) * mm, v(38.2, 18.97) * mm, v(36.9, 15.64) * mm, v(36.07, 13.53) * mm]});
            skFitSpline(sketch, "E478", {"points": [v(36.07, 13.53) * mm, v(34.34, 9.1) * mm, v(33.96, 8.13) * mm, v(33.14, 6.04) * mm]});
            skFitSpline(sketch, "E479", {"points": [v(33.14, 6.04) * mm, v(32.66, 4.8) * mm, v(32.04, 3.23) * mm, v(31.77, 2.54) * mm]});
            skFitSpline(sketch, "E480", {"points": [v(31.77, 2.54) * mm, v(30.46, -0.83) * mm, v(29.93, -2.16) * mm, v(29.87, -2.22) * mm]});
            skFitSpline(sketch, "E481", {"points": [v(29.87, -2.22) * mm, v(29.76, -2.33) * mm, v(30.06, -3) * mm, v(26.01, 6.51) * mm]});
            skFitSpline(sketch, "E482", {"points": [v(26.01, 6.51) * mm, v(25.46, 7.81) * mm, v(24.9, 9.14) * mm, v(24.76, 9.46) * mm]});
            skFitSpline(sketch, "E483", {"points": [v(24.76, 9.46) * mm, v(24.47, 10.12) * mm, v(22.35, 15.11) * mm, v(21.3, 17.56) * mm]});
            skFitSpline(sketch, "E484", {"points": [v(21.3, 17.56) * mm, v(20.93, 18.44) * mm, v(19.97, 20.7) * mm, v(19.17, 22.57) * mm]});
            skFitSpline(sketch, "E485", {"points": [v(19.17, 22.57) * mm, v(17.73, 25.95) * mm, v(17.58, 26.34) * mm, v(17.5, 26.99) * mm]});
            skFitSpline(sketch, "E486", {"points": [v(12.27, 27.32) * mm, v(9.41, 27.32) * mm, v(7.07, 27.3) * mm, v(7.07, 27.27) * mm]});
            skFitSpline(sketch, "E487", {"points": [v(7.07, 27.27) * mm, v(7.07, 27.24) * mm, v(7.23, 27.13) * mm, v(7.42, 27) * mm]});
            skFitSpline(sketch, "E488", {"points": [v(7.42, 27) * mm, v(7.83, 26.76) * mm, v(8.5, 26.05) * mm, v(8.72, 25.65) * mm]});
            skFitSpline(sketch, "E489", {"points": [v(8.72, 25.65) * mm, v(9.14, 24.89) * mm, v(9.24, 23.69) * mm, v(9, 22.16) * mm]});
            skFitSpline(sketch, "E490", {"points": [v(9, 22.16) * mm, v(8.94, 21.74) * mm, v(8.73, 20.22) * mm, v(8.54, 18.79) * mm]});
            skFitSpline(sketch, "E491", {"points": [v(8.54, 18.79) * mm, v(8.23, 16.5) * mm, v(7.9, 14.04) * mm, v(7.16, 8.7) * mm]});
            skFitSpline(sketch, "E492", {"points": [v(7.16, 8.7) * mm, v(7.05, 7.9) * mm, v(6.88, 6.64) * mm, v(6.78, 5.9) * mm]});
            skFitSpline(sketch, "E493", {"points": [v(6.78, 5.9) * mm, v(6.68, 5.16) * mm, v(6.54, 4.1) * mm, v(6.46, 3.53) * mm]});
            skFitSpline(sketch, "E494", {"points": [v(6.46, 3.53) * mm, v(6.33, 2.6) * mm, v(6.03, 0.38) * mm, v(5.55, -3.2) * mm]});
            skFitSpline(sketch, "E495", {"points": [v(5.55, -3.2) * mm, v(5.04, -6.94) * mm, v(4.69, -8.44) * mm, v(3.95, -9.94) * mm]});
            skFitSpline(sketch, "E496", {"points": [v(3.95, -9.94) * mm, v(3.54, -10.77) * mm, v(3.1, -11.4) * mm, v(2.46, -12.05) * mm]});
            skFitSpline(sketch, "E497", {"points": [v(2.46, -12.05) * mm, v(2.24, -12.28) * mm, v(2.07, -12.49) * mm, v(2.09, -12.5) * mm]});
            skFitSpline(sketch, "E498", {"points": [v(2.09, -12.5) * mm, v(2.14, -12.56) * mm, v(11.75, -12.55) * mm, v(11.75, -12.5) * mm]});
            skFitSpline(sketch, "E499", {"points": [v(11.75, -12.5) * mm, v(11.75, -12.47) * mm, v(11.65, -12.4) * mm, v(11.53, -12.34) * mm]});
            skFitSpline(sketch, "E500", {"points": [v(11.53, -12.34) * mm, v(11.14, -12.16) * mm, v(10.58, -11.72) * mm, v(10.34, -11.42) * mm]});
            skFitSpline(sketch, "E501", {"points": [v(10.34, -11.42) * mm, v(9.53, -10.39) * mm, v(9.34, -9.09) * mm, v(9.62, -6.5) * mm]});
            skFitSpline(sketch, "E502", {"points": [v(9.62, -6.5) * mm, v(9.7, -5.78) * mm, v(9.9, -4.33) * mm, v(11.05, 4.4) * mm]});
            skFitSpline(sketch, "E503", {"points": [v(11.05, 4.4) * mm, v(11.3, 6.32) * mm, v(11.74, 9.6) * mm, v(12.02, 11.71) * mm]});
            skFitSpline(sketch, "E504", {"points": [v(12.02, 11.71) * mm, v(13.32, 21.54) * mm, v(13.3, 21.39) * mm, v(13.38, 21.39) * mm]});
            skFitSpline(sketch, "E505", {"points": [v(13.38, 21.39) * mm, v(13.43, 21.39) * mm, v(13.9, 20.36) * mm, v(14.65, 18.55) * mm]});
            skFitSpline(sketch, "E506", {"points": [v(14.65, 18.55) * mm, v(15.3, 17) * mm, v(16.08, 15.17) * mm, v(16.36, 14.5) * mm]});
            skFitSpline(sketch, "E507", {"points": [v(16.36, 14.5) * mm, v(16.65, 13.82) * mm, v(18.43, 9.6) * mm, v(20.31, 5.1) * mm]});
            skFitSpline(sketch, "E508", {"points": [v(20.31, 5.1) * mm, v(25.78, -7.9) * mm, v(25.79, -7.9) * mm, v(26.38, -8.95) * mm]});
            skFitSpline(sketch, "E509", {"points": [v(26.38, -8.95) * mm, v(27.24, -10.47) * mm, v(28.12, -11.5) * mm, v(29.55, -12.7) * mm]});
            skFitSpline(sketch, "E510", {"points": [v(29.55, -12.7) * mm, v(29.97, -13.06) * mm, v(30.2, -13.22) * mm, v(30.23, -13.17) * mm]});
            skFitSpline(sketch, "E511", {"points": [v(30.23, -13.17) * mm, v(30.25, -13.13) * mm, v(30.68, -12.03) * mm, v(31.19, -10.73) * mm]});
            skFitSpline(sketch, "E512", {"points": [v(55.74, -11.44) * mm, v(55.72, -11.4) * mm, v(55.73, -11.37) * mm, v(55.76, -11.35) * mm]});
            skFitSpline(sketch, "E513", {"points": [v(55.76, -11.35) * mm, v(55.78, -11.33) * mm, v(55.8, -11.36) * mm, v(55.8, -11.4) * mm]});
            skFitSpline(sketch, "E514", {"points": [v(55.8, -11.4) * mm, v(55.8, -11.5) * mm, v(55.79, -11.51) * mm, v(55.74, -11.44) * mm]});
            skLineSegment(sketch, "E515.bottom", {"start": v(-59.9, -23.94) * mm, "end": v(59.9, -23.94) * mm});
            skLineSegment(sketch, "E515.top", {"start": v(-58.92, -26.25) * mm, "end": v(58.92, -26.25) * mm});
            skPoint(sketch, "E515.left.start.orphan", {"position": v(-62.63, -23.94) * mm});
            skCircle(sketch, "E516", {"center": v(0, 0) * mm, "radius": 64.5 * mm});
            skSolve(sketch);
        }
        {
            var Q0;
            {var subQ0=sQuery(id+"F0.wireOp",EDGE,"E515.top");Q0=makeQuery(id+"F0.imprint","IMPRINT",FACE,{"disambiguationData":[TD([[makeQuery(id+"F0.imprint","IMPRINT",EDGE,{"derivedFrom":subQ0}),-1.0]])]});}
            var Q1;
            {var subQ0=sQuery(id+"F0.wireOp",EDGE,"E515.top");Q1=makeQuery(id+"F0.imprint","IMPRINT",FACE,{"disambiguationData":[TD([[makeQuery(id+"F0.imprint","IMPRINT",EDGE,{"derivedFrom":subQ0}),1.0]])]});}
            var Q2;
            Q2=makeQuery(id+"F0.imprint","IMPRINT",FACE,{"disambiguationData":[TD([[makeQuery(id+"F0.imprint","IMPRINT",EDGE,{"derivedFrom":sQuery(id+"F0.wireOp",EDGE,"E0")}),1.0]])]});
            var Q3;
            Q3=makeQuery(id+"F0.imprint","IMPRINT",FACE,{"disambiguationData":[TD([[makeQuery(id+"F0.imprint","IMPRINT",EDGE,{"derivedFrom":sQuery(id+"F0.wireOp",EDGE,"E19")}),-1.0]])]});
            var Q4;
            Q4=makeQuery(id+"F0.imprint","IMPRINT",FACE,{"disambiguationData":[TD([[makeQuery(id+"F0.imprint","IMPRINT",EDGE,{"derivedFrom":sQuery(id+"F0.wireOp",EDGE,"E47")}),-1.0]])]});
            var Q5;
            Q5=makeQuery(id+"F0.imprint","IMPRINT",FACE,{"disambiguationData":[TD([[makeQuery(id+"F0.imprint","IMPRINT",EDGE,{"derivedFrom":sQuery(id+"F0.wireOp",EDGE,"E35")}),-1.0]])]});
            var Q6;
            {var subQ1=sQuery(id+"F0.wireOp",EDGE,"E5");Q6=makeQuery(id+"F0.imprint","IMPRINT",FACE,{"disambiguationData":[TD([[makeQuery(id+"F0.imprint","IMPRINT",EDGE,{"derivedFrom":subQ1}),-1.0]])]});}
            var Q7;
            Q7=makeQuery(id+"F0.imprint","IMPRINT",FACE,{"disambiguationData":[TD([[makeQuery(id+"F0.imprint","IMPRINT",EDGE,{"derivedFrom":sQuery(id+"F0.wireOp",EDGE,"E10")}),-1.0]])]});
            var Q8;
            Q8=makeQuery(id+"F0.imprint","IMPRINT",FACE,{"disambiguationData":[TD([[makeQuery(id+"F0.imprint","IMPRINT",EDGE,{"derivedFrom":sQuery(id+"F0.wireOp",EDGE,"E12")}),1.0]])]});
            var Q9;
            {var subQ5=sQuery(id+"F0.wireOp",EDGE,"E86");Q9=makeQuery(id+"F0.imprint","IMPRINT",FACE,{"disambiguationData":[TD([[makeQuery(id+"F0.imprint","IMPRINT",EDGE,{"derivedFrom":subQ5}),-1.0]])]});}
            var Q10;
            {var subQ1=sQuery(id+"F0.wireOp",EDGE,"E32");Q10=makeQuery(id+"F0.imprint","IMPRINT",FACE,{"disambiguationData":[TD([[makeQuery(id+"F0.imprint","IMPRINT",EDGE,{"derivedFrom":subQ1}),-1.0]])]});}
            var Q11;
            {var subQ1=sQuery(id+"F0.wireOp",EDGE,"E331");Q11=makeQuery(id+"F0.imprint","IMPRINT",FACE,{"disambiguationData":[TD([[makeQuery(id+"F0.imprint","IMPRINT",EDGE,{"derivedFrom":subQ1}),-1.0]])]});}
            var Q12;
            Q12=makeQuery(id+"F0.imprint","IMPRINT",FACE,{"disambiguationData":[TD([[makeQuery(id+"F0.imprint","IMPRINT",EDGE,{"derivedFrom":sQuery(id+"F0.wireOp",EDGE,"E38")}),-1.0]])]});
            var Q13;
            Q13=makeQuery(id+"F0.imprint","IMPRINT",FACE,{"disambiguationData":[TD([[makeQuery(id+"F0.imprint","IMPRINT",EDGE,{"derivedFrom":sQuery(id+"F0.wireOp",EDGE,"E283")}),-1.0]])]});
            var Q14;
            {var subQ0=sQuery(id+"F0.wireOp",EDGE,"E22");var subQ1=sQuery(id+"F0.wireOp",EDGE,"E9");var subQ2=makeQuery(id+"F0.imprint","INTERSECT",VERTEX,{"derivedFrom":[subQ1,subQ0]});Q14=makeQuery(id+"F0.imprint","IMPRINT",FACE,{"disambiguationData":[TD([[makeQuery(id+"F0.imprint","IMPRINT",EDGE,{"disambiguationData":[TD([[subQ2,-1.0]])],"derivedFrom":subQ1}),-1.0]])]});}
            var Q15;
            {var subQ5=sQuery(id+"F0.wireOp",EDGE,"E47");Q15=makeQuery(id+"F0.imprint","IMPRINT",FACE,{"disambiguationData":[TD([[makeQuery(id+"F0.imprint","IMPRINT",EDGE,{"derivedFrom":subQ5}),1.0]])]});}
            var Q16;
            {var subQ1=sQuery(id+"F0.wireOp",EDGE,"E41");Q16=makeQuery(id+"F0.imprint","IMPRINT",FACE,{"disambiguationData":[TD([[makeQuery(id+"F0.imprint","IMPRINT",EDGE,{"derivedFrom":subQ1}),-1.0]])]});}
            var Q17;
            {var subQ0=sQuery(id+"F0.wireOp",EDGE,"E258");var subQ1=sQuery(id+"F0.wireOp",EDGE,"E4");var subQ2=makeQuery(id+"F0.imprint","INTERSECT",VERTEX,{"derivedFrom":[subQ1,subQ0]});Q17=makeQuery(id+"F0.imprint","IMPRINT",FACE,{"disambiguationData":[TD([[makeQuery(id+"F0.imprint","IMPRINT",EDGE,{"disambiguationData":[TD([[subQ2,-1.0]])],"derivedFrom":subQ1}),-1.0]])]});}
            var Q18;
            Q18=makeQuery(id+"F0.imprint","IMPRINT",FACE,{"disambiguationData":[TD([[makeQuery(id+"F0.imprint","IMPRINT",EDGE,{"derivedFrom":sQuery(id+"F0.wireOp",EDGE,"E13")}),-1.0]])]});
            var Q19;
            Q19=makeQuery(id+"F0.imprint","IMPRINT",FACE,{"disambiguationData":[TD([[makeQuery(id+"F0.imprint","IMPRINT",EDGE,{"derivedFrom":sQuery(id+"F0.wireOp",EDGE,"E17")}),1.0]])]});
            var Q20;
            {var subQ0=sQuery(id+"F0.wireOp",EDGE,"E45");var subQ1=sQuery(id+"F0.wireOp",EDGE,"E34");var subQ2=makeQuery(id+"F0.imprint","INTERSECT",VERTEX,{"derivedFrom":[subQ1,subQ0]});Q20=makeQuery(id+"F0.imprint","IMPRINT",FACE,{"disambiguationData":[TD([[makeQuery(id+"F0.imprint","IMPRINT",EDGE,{"disambiguationData":[TD([[subQ2,-1.0]])],"derivedFrom":subQ1}),-1.0]])]});}
            var Q21;
            {var subQ0=sQuery(id+"F0.wireOp",EDGE,"E461");var subQ1=sQuery(id+"F0.wireOp",EDGE,"E43");var subQ2=makeQuery(id+"F0.imprint","INTERSECT",VERTEX,{"derivedFrom":[subQ1,subQ0]});Q21=makeQuery(id+"F0.imprint","IMPRINT",FACE,{"disambiguationData":[TD([[makeQuery(id+"F0.imprint","IMPRINT",EDGE,{"disambiguationData":[TD([[subQ2,-1.0]])],"derivedFrom":subQ1}),-1.0]])]});}
            var Q22;
            {var subQ7=sQuery(id+"F0.wireOp",EDGE,"E0");Q22=makeQuery(id+"F0.imprint","IMPRINT",FACE,{"disambiguationData":[TD([[makeQuery(id+"F0.imprint","IMPRINT",EDGE,{"derivedFrom":subQ7}),-1.0]])]});}
            var Q23;
            {var subQ5=sQuery(id+"F0.wireOp",EDGE,"E21");Q23=makeQuery(id+"F0.imprint","IMPRINT",FACE,{"disambiguationData":[TD([[makeQuery(id+"F0.imprint","IMPRINT",EDGE,{"derivedFrom":subQ5}),1.0]])]});}
            var Q24;
            {var subQ0=sQuery(id+"F0.wireOp",EDGE,"E498");var subQ1=sQuery(id+"F0.wireOp",EDGE,"E31");var subQ2=makeQuery(id+"F0.imprint","INTERSECT",VERTEX,{"disambiguationData":[OD(0.0)],"derivedFrom":[subQ1,subQ0]});Q24=makeQuery(id+"F0.imprint","IMPRINT",FACE,{"disambiguationData":[TD([[makeQuery(id+"F0.imprint","IMPRINT",EDGE,{"disambiguationData":[TD([[subQ2,-1.0]])],"derivedFrom":subQ1}),-1.0]])]});}
            var Q25;
            {var subQ0=sQuery(id+"F0.wireOp",EDGE,"E20");var subQ1=sQuery(id+"F0.wireOp",EDGE,"E9");var subQ2=makeQuery(id+"F0.imprint","INTERSECT",VERTEX,{"derivedFrom":[subQ1,subQ0]});Q25=makeQuery(id+"F0.imprint","IMPRINT",FACE,{"disambiguationData":[TD([[makeQuery(id+"F0.imprint","IMPRINT",EDGE,{"disambiguationData":[TD([[subQ2,-1.0]])],"derivedFrom":subQ1}),1.0]])]});}
            var Q26;
            {var subQ1=sQuery(id+"F0.wireOp",EDGE,"E27");Q26=makeQuery(id+"F0.imprint","IMPRINT",FACE,{"disambiguationData":[TD([[makeQuery(id+"F0.imprint","IMPRINT",EDGE,{"derivedFrom":subQ1}),-1.0]])]});}
            var Q27;
            Q27=makeQuery(id+"F0.imprint","IMPRINT",FACE,{"disambiguationData":[TD([[makeQuery(id+"F0.imprint","IMPRINT",EDGE,{"derivedFrom":sQuery(id+"F0.wireOp",EDGE,"E23")}),1.0]])]});
            var Q28;
            Q28=makeQuery(id+"F0.imprint","IMPRINT",FACE,{"disambiguationData":[TD([[makeQuery(id+"F0.imprint","IMPRINT",EDGE,{"derivedFrom":sQuery(id+"F0.wireOp",EDGE,"E35")}),1.0]])]});
            var Q29;
            Q29=makeQuery(id+"F0.imprint","IMPRINT",FACE,{"disambiguationData":[TD([[makeQuery(id+"F0.imprint","IMPRINT",EDGE,{"derivedFrom":sQuery(id+"F0.wireOp",EDGE,"E512")}),-1.0]])]});
            extrude(context, id + "F1", {"entities" : qUnion([Q0, Q1, Q2, Q3, Q4, Q5, Q6, Q7, Q8, Q9, Q10, Q11, Q12, Q13, Q14, Q15, Q16, Q17, Q18, Q19, Q20, Q21, Q22, Q23, Q24, Q25, Q26, Q27, Q28, Q29]), "depth" : 3 * mm, "offsetDistance" : 25 * mm});
        }
        {
            var Q0;
            Q0=makeQuery(id+"F0.imprint","IMPRINT",FACE,{"disambiguationData":[TD([[makeQuery(id+"F0.imprint","IMPRINT",EDGE,{"derivedFrom":sQuery(id+"F0.wireOp",EDGE,"E19")}),-1.0]])]});
            var Q1;
            Q1=makeQuery(id+"F0.imprint","IMPRINT",FACE,{"disambiguationData":[TD([[makeQuery(id+"F0.imprint","IMPRINT",EDGE,{"derivedFrom":sQuery(id+"F0.wireOp",EDGE,"E47")}),-1.0]])]});
            var Q2;
            {var subQ0=sQuery(id+"F0.wireOp",EDGE,"E515.top");Q2=makeQuery(id+"F0.imprint","IMPRINT",FACE,{"disambiguationData":[TD([[makeQuery(id+"F0.imprint","IMPRINT",EDGE,{"derivedFrom":subQ0}),1.0]])]});}
            extrude(context, id + "F2", {"entities" : qUnion([Q0, Q1, Q2]), "operationType" : NewBodyOperationType.ADD, "depth" : 6 * mm, "offsetDistance" : 25 * mm});
        }
        {
            var Q0;
            {var subQ0=sQuery(id+"F0.wireOp",EDGE,"E516");var subQ1=sQuery(id+"F0.wireOp",EDGE,"E515.bottom");Q0=makeQuery(id+"F2.boolean.opBoolean","SPLIT",EDGE,{"disambiguationData":[TD([makeQuery(id+"F2.opExtrude","SWEPT_FACE",FACE,{"disambiguationData":[OSD([subQ1])]})])],"derivedFrom":makeQuery(id+"F1.opExtrude","CAP_EDGE",EDGE,{"disambiguationData":[OSD([subQ0])],"isStart":false})});}
            var Q1;
            {var subQ0=sQuery(id+"F0.wireOp",EDGE,"E516");var subQ2=sQuery(id+"F0.wireOp",EDGE,"E515.top");Q1=makeQuery(id+"F2.boolean.opBoolean","SPLIT",EDGE,{"disambiguationData":[TD([makeQuery(id+"F2.opExtrude","SWEPT_FACE",FACE,{"disambiguationData":[OSD([subQ2])]})])],"derivedFrom":makeQuery(id+"F1.opExtrude","CAP_EDGE",EDGE,{"disambiguationData":[OSD([subQ0])],"isStart":false})});}
            fillet(context, id + "F3", {"entities" : qUnion([Q0, Q1]), "radius" : 1 * mm, "tangentPropagation" : true, "allowEdgeOverflow" : false});
        }
        {
            var Q0;
            Q0=makeQuery(id+"F0.imprint","IMPRINT",FACE,{"disambiguationData":[TD([[makeQuery(id+"F0.imprint","IMPRINT",EDGE,{"derivedFrom":sQuery(id+"F0.wireOp",EDGE,"E0")}),1.0]])]});
            var sketch = newSketch(context, id + "F4", { "sketchPlane" : qUnion([Q0])});
            skLineSegment(sketch, "E517.bottom", {"start": v(0, 69.5) * mm, "end": v(1, 69.5) * mm});
            skLineSegment(sketch, "E517.top", {"start": v(0, 49.5) * mm, "end": v(1, 49.5) * mm});
            skLineSegment(sketch, "E517.left", {"start": v(0, 69.5) * mm, "end": v(0, 49.5) * mm});
            skLineSegment(sketch, "E517.right", {"start": v(1, 69.5) * mm, "end": v(1, 49.5) * mm});
            skLineSegment(sketch, "E518.MirrorCS", {"start": v(0, -49.5) * mm, "end": v(1, -49.5) * mm});
            skLineSegment(sketch, "E519.MirrorCS", {"start": v(0, -69.5) * mm, "end": v(1, -69.5) * mm});
            skLineSegment(sketch, "E520.MirrorCS", {"start": v(0, -69.5) * mm, "end": v(0, -49.5) * mm});
            skLineSegment(sketch, "E521.MirrorCS", {"start": v(1, -69.5) * mm, "end": v(1, -49.5) * mm});
            skSolve(sketch);
        }
        {
            var Q0;
            Q0 = qSketchRegion(id + "F4", true);
            var Q1;
            Q1=sQuery(id+"F4.wireOp",EDGE,"E517.left");
            revolve(context, id + "F5", {"operationType" : NewBodyOperationType.REMOVE, "surfaceOperationType" : NewSurfaceOperationType.NEW, "entities" : qUnion([Q0]), "axis" : qUnion([Q1]), "revolveType" : RevolveType.FULL, "oppositeDirection" : true});
        }
    });
